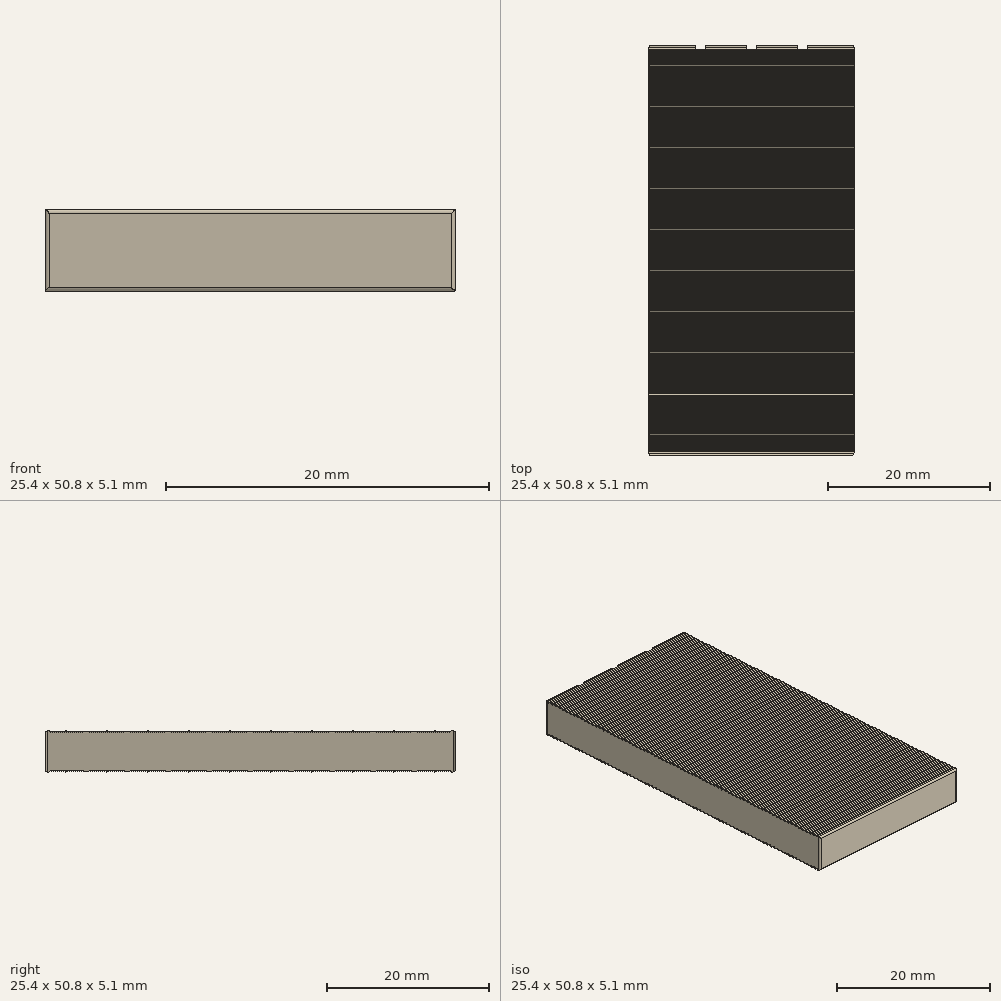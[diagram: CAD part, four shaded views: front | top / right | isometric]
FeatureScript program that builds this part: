
annotation { "Feature Type Name" : "Feature", "Feature Type Description" : "" }
export const myFeature = defineFeature(function(context is Context, id is Id, definition is map)
    precondition{}
    {
        {
            var Q0;
            Q0=qCreatedBy(makeId("Front.planeOp"),FACE);
            var sketch = newSketch(context, id + "F0", { "sketchPlane" : qUnion([Q0])});
            skLineSegment(sketch, "E0.bottom", {"start": v(12.7, -2.54) * mm, "end": v(-12.7, -2.54) * mm});
            skLineSegment(sketch, "E0.top", {"start": v(12.7, 2.54) * mm, "end": v(-12.7, 2.54) * mm});
            skLineSegment(sketch, "E0.left", {"start": v(12.7, -2.54) * mm, "end": v(12.7, 2.54) * mm});
            skLineSegment(sketch, "E0.right", {"start": v(-12.7, -2.54) * mm, "end": v(-12.7, 2.54) * mm});
            skPoint(sketch, "E0.middle", {"position": v(0, 0) * mm});
            skSolve(sketch);
        }
        {
            var Q0;
            Q0 = qSketchRegion(id + "F0", true);
            extrude(context, id + "F1", {"entities" : qUnion([Q0]), "endBound" : BoundingType.SYMMETRIC, "depth" : 50.8 * mm, "offsetDistance" : 25.4 * mm});
        }
        {
            var Q0;
            Q0=qCreatedBy(makeId("Right.planeOp"),FACE);
            var sketch = newSketch(context, id + "F2", { "sketchPlane" : qUnion([Q0])});
            skLineSegment(sketch, "E1", {"start": v(0, -2.54) * mm, "end": v(-0.13, -2.32) * mm});
            skLineSegment(sketch, "E2", {"start": v(-0.13, -2.32) * mm, "end": v(-0.25, -2.54) * mm});
            skLineSegment(sketch, "E3.1.0.0", {"start": v(0.25, -2.54) * mm, "end": v(0.13, -2.32) * mm});
            skLineSegment(sketch, "E3.1.0.1", {"start": v(0.13, -2.32) * mm, "end": v(0, -2.54) * mm});
            skLineSegment(sketch, "E3.2.0.0", {"start": v(0.5, -2.54) * mm, "end": v(0.38, -2.32) * mm});
            skLineSegment(sketch, "E3.2.0.1", {"start": v(0.38, -2.32) * mm, "end": v(0.25, -2.54) * mm});
            skLineSegment(sketch, "E3.3.0.0", {"start": v(0.76, -2.54) * mm, "end": v(0.64, -2.32) * mm});
            skLineSegment(sketch, "E3.3.0.1", {"start": v(0.64, -2.32) * mm, "end": v(0.5, -2.54) * mm});
            skLineSegment(sketch, "E3.4.0.0", {"start": v(1.02, -2.54) * mm, "end": v(0.89, -2.32) * mm});
            skLineSegment(sketch, "E3.4.0.1", {"start": v(0.89, -2.32) * mm, "end": v(0.76, -2.54) * mm});
            skLineSegment(sketch, "E3.5.0.0", {"start": v(1.27, -2.54) * mm, "end": v(1.14, -2.32) * mm});
            skLineSegment(sketch, "E3.5.0.1", {"start": v(1.14, -2.32) * mm, "end": v(1.02, -2.54) * mm});
            skLineSegment(sketch, "E3.6.0.0", {"start": v(1.52, -2.54) * mm, "end": v(1.4, -2.32) * mm});
            skLineSegment(sketch, "E3.6.0.1", {"start": v(1.4, -2.32) * mm, "end": v(1.27, -2.54) * mm});
            skLineSegment(sketch, "E3.7.0.0", {"start": v(1.78, -2.54) * mm, "end": v(1.65, -2.32) * mm});
            skLineSegment(sketch, "E3.7.0.1", {"start": v(1.65, -2.32) * mm, "end": v(1.52, -2.54) * mm});
            skLineSegment(sketch, "E3.8.0.0", {"start": v(2.03, -2.54) * mm, "end": v(1.9, -2.32) * mm});
            skLineSegment(sketch, "E3.8.0.1", {"start": v(1.9, -2.32) * mm, "end": v(1.78, -2.54) * mm});
            skLineSegment(sketch, "E3.9.0.0", {"start": v(2.29, -2.54) * mm, "end": v(2.16, -2.32) * mm});
            skLineSegment(sketch, "E3.9.0.1", {"start": v(2.16, -2.32) * mm, "end": v(2.03, -2.54) * mm});
            skLineSegment(sketch, "E3.10.0.0", {"start": v(2.54, -2.54) * mm, "end": v(2.41, -2.32) * mm});
            skLineSegment(sketch, "E3.10.0.1", {"start": v(2.41, -2.32) * mm, "end": v(2.29, -2.54) * mm});
            skLineSegment(sketch, "E3.11.0.0", {"start": v(2.8, -2.54) * mm, "end": v(2.67, -2.32) * mm});
            skLineSegment(sketch, "E3.11.0.1", {"start": v(2.67, -2.32) * mm, "end": v(2.54, -2.54) * mm});
            skLineSegment(sketch, "E3.12.0.0", {"start": v(3.05, -2.54) * mm, "end": v(2.92, -2.32) * mm});
            skLineSegment(sketch, "E3.12.0.1", {"start": v(2.92, -2.32) * mm, "end": v(2.8, -2.54) * mm});
            skLineSegment(sketch, "E3.13.0.0", {"start": v(3.3, -2.54) * mm, "end": v(3.18, -2.32) * mm});
            skLineSegment(sketch, "E3.13.0.1", {"start": v(3.18, -2.32) * mm, "end": v(3.05, -2.54) * mm});
            skLineSegment(sketch, "E3.14.0.0", {"start": v(3.56, -2.54) * mm, "end": v(3.43, -2.32) * mm});
            skLineSegment(sketch, "E3.14.0.1", {"start": v(3.43, -2.32) * mm, "end": v(3.3, -2.54) * mm});
            skLineSegment(sketch, "E3.15.0.0", {"start": v(3.81, -2.54) * mm, "end": v(3.68, -2.32) * mm});
            skLineSegment(sketch, "E3.15.0.1", {"start": v(3.68, -2.32) * mm, "end": v(3.56, -2.54) * mm});
            skLineSegment(sketch, "E3.16.0.0", {"start": v(4.06, -2.54) * mm, "end": v(3.94, -2.32) * mm});
            skLineSegment(sketch, "E3.16.0.1", {"start": v(3.94, -2.32) * mm, "end": v(3.81, -2.54) * mm});
            skLineSegment(sketch, "E3.17.0.0", {"start": v(4.32, -2.54) * mm, "end": v(4.2, -2.32) * mm});
            skLineSegment(sketch, "E3.17.0.1", {"start": v(4.2, -2.32) * mm, "end": v(4.06, -2.54) * mm});
            skLineSegment(sketch, "E3.18.0.0", {"start": v(4.57, -2.54) * mm, "end": v(4.45, -2.32) * mm});
            skLineSegment(sketch, "E3.18.0.1", {"start": v(4.45, -2.32) * mm, "end": v(4.32, -2.54) * mm});
            skLineSegment(sketch, "E3.19.0.0", {"start": v(4.83, -2.54) * mm, "end": v(4.7, -2.32) * mm});
            skLineSegment(sketch, "E3.19.0.1", {"start": v(4.7, -2.32) * mm, "end": v(4.57, -2.54) * mm});
            skLineSegment(sketch, "E3.20.0.0", {"start": v(5.08, -2.54) * mm, "end": v(4.95, -2.32) * mm});
            skLineSegment(sketch, "E3.20.0.1", {"start": v(4.95, -2.32) * mm, "end": v(4.83, -2.54) * mm});
            skLineSegment(sketch, "E3.21.0.0", {"start": v(5.33, -2.54) * mm, "end": v(5.2, -2.32) * mm});
            skLineSegment(sketch, "E3.21.0.1", {"start": v(5.2, -2.32) * mm, "end": v(5.08, -2.54) * mm});
            skLineSegment(sketch, "E3.22.0.0", {"start": v(5.59, -2.54) * mm, "end": v(5.46, -2.32) * mm});
            skLineSegment(sketch, "E3.22.0.1", {"start": v(5.46, -2.32) * mm, "end": v(5.33, -2.54) * mm});
            skLineSegment(sketch, "E3.23.0.0", {"start": v(5.84, -2.54) * mm, "end": v(5.72, -2.32) * mm});
            skLineSegment(sketch, "E3.23.0.1", {"start": v(5.72, -2.32) * mm, "end": v(5.59, -2.54) * mm});
            skLineSegment(sketch, "E3.24.0.0", {"start": v(6.1, -2.54) * mm, "end": v(5.97, -2.32) * mm});
            skLineSegment(sketch, "E3.24.0.1", {"start": v(5.97, -2.32) * mm, "end": v(5.84, -2.54) * mm});
            skLineSegment(sketch, "E3.25.0.0", {"start": v(6.35, -2.54) * mm, "end": v(6.22, -2.32) * mm});
            skLineSegment(sketch, "E3.25.0.1", {"start": v(6.22, -2.32) * mm, "end": v(6.1, -2.54) * mm});
            skLineSegment(sketch, "E3.26.0.0", {"start": v(6.6, -2.54) * mm, "end": v(6.48, -2.32) * mm});
            skLineSegment(sketch, "E3.26.0.1", {"start": v(6.48, -2.32) * mm, "end": v(6.35, -2.54) * mm});
            skLineSegment(sketch, "E3.27.0.0", {"start": v(6.86, -2.54) * mm, "end": v(6.73, -2.32) * mm});
            skLineSegment(sketch, "E3.27.0.1", {"start": v(6.73, -2.32) * mm, "end": v(6.6, -2.54) * mm});
            skLineSegment(sketch, "E3.28.0.0", {"start": v(7.11, -2.54) * mm, "end": v(6.99, -2.32) * mm});
            skLineSegment(sketch, "E3.28.0.1", {"start": v(6.99, -2.32) * mm, "end": v(6.86, -2.54) * mm});
            skLineSegment(sketch, "E3.29.0.0", {"start": v(7.37, -2.54) * mm, "end": v(7.24, -2.32) * mm});
            skLineSegment(sketch, "E3.29.0.1", {"start": v(7.24, -2.32) * mm, "end": v(7.11, -2.54) * mm});
            skLineSegment(sketch, "E3.30.0.0", {"start": v(7.62, -2.54) * mm, "end": v(7.5, -2.32) * mm});
            skLineSegment(sketch, "E3.30.0.1", {"start": v(7.5, -2.32) * mm, "end": v(7.37, -2.54) * mm});
            skLineSegment(sketch, "E3.31.0.0", {"start": v(7.87, -2.54) * mm, "end": v(7.75, -2.32) * mm});
            skLineSegment(sketch, "E3.31.0.1", {"start": v(7.75, -2.32) * mm, "end": v(7.62, -2.54) * mm});
            skLineSegment(sketch, "E3.32.0.0", {"start": v(8.13, -2.54) * mm, "end": v(8, -2.32) * mm});
            skLineSegment(sketch, "E3.32.0.1", {"start": v(8, -2.32) * mm, "end": v(7.87, -2.54) * mm});
            skLineSegment(sketch, "E3.33.0.0", {"start": v(8.38, -2.54) * mm, "end": v(8.26, -2.32) * mm});
            skLineSegment(sketch, "E3.33.0.1", {"start": v(8.26, -2.32) * mm, "end": v(8.13, -2.54) * mm});
            skLineSegment(sketch, "E3.34.0.0", {"start": v(8.64, -2.54) * mm, "end": v(8.5, -2.32) * mm});
            skLineSegment(sketch, "E3.34.0.1", {"start": v(8.5, -2.32) * mm, "end": v(8.38, -2.54) * mm});
            skLineSegment(sketch, "E3.35.0.0", {"start": v(8.9, -2.54) * mm, "end": v(8.76, -2.32) * mm});
            skLineSegment(sketch, "E3.35.0.1", {"start": v(8.76, -2.32) * mm, "end": v(8.64, -2.54) * mm});
            skLineSegment(sketch, "E3.36.0.0", {"start": v(9.14, -2.54) * mm, "end": v(9.02, -2.32) * mm});
            skLineSegment(sketch, "E3.36.0.1", {"start": v(9.02, -2.32) * mm, "end": v(8.9, -2.54) * mm});
            skLineSegment(sketch, "E3.37.0.0", {"start": v(9.4, -2.54) * mm, "end": v(9.27, -2.32) * mm});
            skLineSegment(sketch, "E3.37.0.1", {"start": v(9.27, -2.32) * mm, "end": v(9.14, -2.54) * mm});
            skLineSegment(sketch, "E3.38.0.0", {"start": v(9.65, -2.54) * mm, "end": v(9.53, -2.32) * mm});
            skLineSegment(sketch, "E3.38.0.1", {"start": v(9.53, -2.32) * mm, "end": v(9.4, -2.54) * mm});
            skLineSegment(sketch, "E3.39.0.0", {"start": v(9.9, -2.54) * mm, "end": v(9.78, -2.32) * mm});
            skLineSegment(sketch, "E3.39.0.1", {"start": v(9.78, -2.32) * mm, "end": v(9.65, -2.54) * mm});
            skLineSegment(sketch, "E3.40.0.0", {"start": v(10.16, -2.54) * mm, "end": v(10.03, -2.32) * mm});
            skLineSegment(sketch, "E3.40.0.1", {"start": v(10.03, -2.32) * mm, "end": v(9.9, -2.54) * mm});
            skLineSegment(sketch, "E3.41.0.0", {"start": v(10.41, -2.54) * mm, "end": v(10.29, -2.32) * mm});
            skLineSegment(sketch, "E3.41.0.1", {"start": v(10.29, -2.32) * mm, "end": v(10.16, -2.54) * mm});
            skLineSegment(sketch, "E3.42.0.0", {"start": v(10.67, -2.54) * mm, "end": v(10.54, -2.32) * mm});
            skLineSegment(sketch, "E3.42.0.1", {"start": v(10.54, -2.32) * mm, "end": v(10.41, -2.54) * mm});
            skLineSegment(sketch, "E3.43.0.0", {"start": v(10.92, -2.54) * mm, "end": v(10.8, -2.32) * mm});
            skLineSegment(sketch, "E3.43.0.1", {"start": v(10.8, -2.32) * mm, "end": v(10.67, -2.54) * mm});
            skLineSegment(sketch, "E3.44.0.0", {"start": v(11.18, -2.54) * mm, "end": v(11.05, -2.32) * mm});
            skLineSegment(sketch, "E3.44.0.1", {"start": v(11.05, -2.32) * mm, "end": v(10.92, -2.54) * mm});
            skLineSegment(sketch, "E3.45.0.0", {"start": v(11.43, -2.54) * mm, "end": v(11.3, -2.32) * mm});
            skLineSegment(sketch, "E3.45.0.1", {"start": v(11.3, -2.32) * mm, "end": v(11.18, -2.54) * mm});
            skLineSegment(sketch, "E3.46.0.0", {"start": v(11.68, -2.54) * mm, "end": v(11.56, -2.32) * mm});
            skLineSegment(sketch, "E3.46.0.1", {"start": v(11.56, -2.32) * mm, "end": v(11.43, -2.54) * mm});
            skLineSegment(sketch, "E3.47.0.0", {"start": v(11.94, -2.54) * mm, "end": v(11.81, -2.32) * mm});
            skLineSegment(sketch, "E3.47.0.1", {"start": v(11.81, -2.32) * mm, "end": v(11.68, -2.54) * mm});
            skLineSegment(sketch, "E3.48.0.0", {"start": v(12.2, -2.54) * mm, "end": v(12.07, -2.32) * mm});
            skLineSegment(sketch, "E3.48.0.1", {"start": v(12.07, -2.32) * mm, "end": v(11.94, -2.54) * mm});
            skLineSegment(sketch, "E3.49.0.0", {"start": v(12.45, -2.54) * mm, "end": v(12.32, -2.32) * mm});
            skLineSegment(sketch, "E3.49.0.1", {"start": v(12.32, -2.32) * mm, "end": v(12.2, -2.54) * mm});
            skLineSegment(sketch, "E3.direction1", {"start": v(-0.25, -2.54) * mm, "end": v(0, -2.54) * mm, "construction": true});
            skLineSegment(sketch, "E4.0.50.0", {"start": v(12.7, -2.54) * mm, "end": v(12.57, -2.32) * mm});
            skLineSegment(sketch, "E4.3.50.0", {"start": v(12.57, -2.32) * mm, "end": v(12.45, -2.54) * mm});
            skLineSegment(sketch, "E4.0.51.0", {"start": v(12.95, -2.54) * mm, "end": v(12.83, -2.32) * mm});
            skLineSegment(sketch, "E4.3.51.0", {"start": v(12.83, -2.32) * mm, "end": v(12.7, -2.54) * mm});
            skLineSegment(sketch, "E4.0.52.0", {"start": v(13.2, -2.54) * mm, "end": v(13.08, -2.32) * mm});
            skLineSegment(sketch, "E4.3.52.0", {"start": v(13.08, -2.32) * mm, "end": v(12.95, -2.54) * mm});
            skLineSegment(sketch, "E4.0.53.0", {"start": v(13.46, -2.54) * mm, "end": v(13.34, -2.32) * mm});
            skLineSegment(sketch, "E4.3.53.0", {"start": v(13.34, -2.32) * mm, "end": v(13.2, -2.54) * mm});
            skLineSegment(sketch, "E4.0.54.0", {"start": v(13.72, -2.54) * mm, "end": v(13.59, -2.32) * mm});
            skLineSegment(sketch, "E4.3.54.0", {"start": v(13.59, -2.32) * mm, "end": v(13.46, -2.54) * mm});
            skLineSegment(sketch, "E4.0.55.0", {"start": v(13.97, -2.54) * mm, "end": v(13.84, -2.32) * mm});
            skLineSegment(sketch, "E4.3.55.0", {"start": v(13.84, -2.32) * mm, "end": v(13.72, -2.54) * mm});
            skLineSegment(sketch, "E4.0.56.0", {"start": v(14.22, -2.54) * mm, "end": v(14.1, -2.32) * mm});
            skLineSegment(sketch, "E4.3.56.0", {"start": v(14.1, -2.32) * mm, "end": v(13.97, -2.54) * mm});
            skLineSegment(sketch, "E4.0.57.0", {"start": v(14.48, -2.54) * mm, "end": v(14.35, -2.32) * mm});
            skLineSegment(sketch, "E4.3.57.0", {"start": v(14.35, -2.32) * mm, "end": v(14.22, -2.54) * mm});
            skLineSegment(sketch, "E4.0.58.0", {"start": v(14.73, -2.54) * mm, "end": v(14.6, -2.32) * mm});
            skLineSegment(sketch, "E4.3.58.0", {"start": v(14.6, -2.32) * mm, "end": v(14.48, -2.54) * mm});
            skLineSegment(sketch, "E4.0.59.0", {"start": v(14.99, -2.54) * mm, "end": v(14.86, -2.32) * mm});
            skLineSegment(sketch, "E4.3.59.0", {"start": v(14.86, -2.32) * mm, "end": v(14.73, -2.54) * mm});
            skLineSegment(sketch, "E4.0.60.0", {"start": v(15.24, -2.54) * mm, "end": v(15.11, -2.32) * mm});
            skLineSegment(sketch, "E4.3.60.0", {"start": v(15.11, -2.32) * mm, "end": v(14.99, -2.54) * mm});
            skLineSegment(sketch, "E4.0.61.0", {"start": v(15.5, -2.54) * mm, "end": v(15.37, -2.32) * mm});
            skLineSegment(sketch, "E4.3.61.0", {"start": v(15.37, -2.32) * mm, "end": v(15.24, -2.54) * mm});
            skLineSegment(sketch, "E4.0.62.0", {"start": v(15.75, -2.54) * mm, "end": v(15.62, -2.32) * mm});
            skLineSegment(sketch, "E4.3.62.0", {"start": v(15.62, -2.32) * mm, "end": v(15.5, -2.54) * mm});
            skLineSegment(sketch, "E4.0.63.0", {"start": v(16, -2.54) * mm, "end": v(15.88, -2.32) * mm});
            skLineSegment(sketch, "E4.3.63.0", {"start": v(15.88, -2.32) * mm, "end": v(15.75, -2.54) * mm});
            skLineSegment(sketch, "E4.0.64.0", {"start": v(16.26, -2.54) * mm, "end": v(16.13, -2.32) * mm});
            skLineSegment(sketch, "E4.3.64.0", {"start": v(16.13, -2.32) * mm, "end": v(16, -2.54) * mm});
            skLineSegment(sketch, "E4.0.65.0", {"start": v(16.51, -2.54) * mm, "end": v(16.38, -2.32) * mm});
            skLineSegment(sketch, "E4.3.65.0", {"start": v(16.38, -2.32) * mm, "end": v(16.26, -2.54) * mm});
            skLineSegment(sketch, "E4.0.66.0", {"start": v(16.76, -2.54) * mm, "end": v(16.64, -2.32) * mm});
            skLineSegment(sketch, "E4.3.66.0", {"start": v(16.64, -2.32) * mm, "end": v(16.51, -2.54) * mm});
            skLineSegment(sketch, "E4.0.67.0", {"start": v(17.02, -2.54) * mm, "end": v(16.9, -2.32) * mm});
            skLineSegment(sketch, "E4.3.67.0", {"start": v(16.9, -2.32) * mm, "end": v(16.76, -2.54) * mm});
            skLineSegment(sketch, "E4.0.68.0", {"start": v(17.27, -2.54) * mm, "end": v(17.15, -2.32) * mm});
            skLineSegment(sketch, "E4.3.68.0", {"start": v(17.15, -2.32) * mm, "end": v(17.02, -2.54) * mm});
            skLineSegment(sketch, "E4.0.69.0", {"start": v(17.53, -2.54) * mm, "end": v(17.4, -2.32) * mm});
            skLineSegment(sketch, "E4.3.69.0", {"start": v(17.4, -2.32) * mm, "end": v(17.27, -2.54) * mm});
            skLineSegment(sketch, "E4.0.70.0", {"start": v(17.78, -2.54) * mm, "end": v(17.65, -2.32) * mm});
            skLineSegment(sketch, "E4.3.70.0", {"start": v(17.65, -2.32) * mm, "end": v(17.53, -2.54) * mm});
            skLineSegment(sketch, "E4.0.71.0", {"start": v(18.03, -2.54) * mm, "end": v(17.9, -2.32) * mm});
            skLineSegment(sketch, "E4.3.71.0", {"start": v(17.9, -2.32) * mm, "end": v(17.78, -2.54) * mm});
            skLineSegment(sketch, "E4.0.72.0", {"start": v(18.29, -2.54) * mm, "end": v(18.16, -2.32) * mm});
            skLineSegment(sketch, "E4.3.72.0", {"start": v(18.16, -2.32) * mm, "end": v(18.03, -2.54) * mm});
            skLineSegment(sketch, "E4.0.73.0", {"start": v(18.54, -2.54) * mm, "end": v(18.42, -2.32) * mm});
            skLineSegment(sketch, "E4.3.73.0", {"start": v(18.42, -2.32) * mm, "end": v(18.29, -2.54) * mm});
            skLineSegment(sketch, "E4.0.74.0", {"start": v(18.8, -2.54) * mm, "end": v(18.67, -2.32) * mm});
            skLineSegment(sketch, "E4.3.74.0", {"start": v(18.67, -2.32) * mm, "end": v(18.54, -2.54) * mm});
            skLineSegment(sketch, "E5.0.75.0", {"start": v(19.05, -2.54) * mm, "end": v(18.92, -2.32) * mm});
            skLineSegment(sketch, "E5.3.75.0", {"start": v(18.92, -2.32) * mm, "end": v(18.8, -2.54) * mm});
            skLineSegment(sketch, "E5.0.76.0", {"start": v(19.3, -2.54) * mm, "end": v(19.18, -2.32) * mm});
            skLineSegment(sketch, "E5.3.76.0", {"start": v(19.18, -2.32) * mm, "end": v(19.05, -2.54) * mm});
            skLineSegment(sketch, "E6.1.0.0", {"start": v(-0.25, -2.54) * mm, "end": v(-0.38, -2.32) * mm});
            skLineSegment(sketch, "E6.1.0.1", {"start": v(-0.38, -2.32) * mm, "end": v(-0.5, -2.54) * mm});
            skLineSegment(sketch, "E6.2.0.0", {"start": v(-0.5, -2.54) * mm, "end": v(-0.63, -2.32) * mm});
            skLineSegment(sketch, "E6.2.0.1", {"start": v(-0.63, -2.32) * mm, "end": v(-0.76, -2.54) * mm});
            skLineSegment(sketch, "E6.3.0.0", {"start": v(-0.76, -2.54) * mm, "end": v(-0.89, -2.32) * mm});
            skLineSegment(sketch, "E6.3.0.1", {"start": v(-0.89, -2.32) * mm, "end": v(-1.02, -2.54) * mm});
            skLineSegment(sketch, "E6.4.0.0", {"start": v(-1.02, -2.54) * mm, "end": v(-1.14, -2.32) * mm});
            skLineSegment(sketch, "E6.4.0.1", {"start": v(-1.14, -2.32) * mm, "end": v(-1.27, -2.54) * mm});
            skLineSegment(sketch, "E6.5.0.0", {"start": v(-1.27, -2.54) * mm, "end": v(-1.4, -2.32) * mm});
            skLineSegment(sketch, "E6.5.0.1", {"start": v(-1.4, -2.32) * mm, "end": v(-1.52, -2.54) * mm});
            skLineSegment(sketch, "E6.6.0.0", {"start": v(-1.52, -2.54) * mm, "end": v(-1.65, -2.32) * mm});
            skLineSegment(sketch, "E6.6.0.1", {"start": v(-1.65, -2.32) * mm, "end": v(-1.78, -2.54) * mm});
            skLineSegment(sketch, "E6.7.0.0", {"start": v(-1.78, -2.54) * mm, "end": v(-1.9, -2.32) * mm});
            skLineSegment(sketch, "E6.7.0.1", {"start": v(-1.9, -2.32) * mm, "end": v(-2.03, -2.54) * mm});
            skLineSegment(sketch, "E6.8.0.0", {"start": v(-2.03, -2.54) * mm, "end": v(-2.16, -2.32) * mm});
            skLineSegment(sketch, "E6.8.0.1", {"start": v(-2.16, -2.32) * mm, "end": v(-2.29, -2.54) * mm});
            skLineSegment(sketch, "E6.9.0.0", {"start": v(-2.29, -2.54) * mm, "end": v(-2.41, -2.32) * mm});
            skLineSegment(sketch, "E6.9.0.1", {"start": v(-2.41, -2.32) * mm, "end": v(-2.54, -2.54) * mm});
            skLineSegment(sketch, "E6.10.0.0", {"start": v(-2.54, -2.54) * mm, "end": v(-2.67, -2.32) * mm});
            skLineSegment(sketch, "E6.10.0.1", {"start": v(-2.67, -2.32) * mm, "end": v(-2.8, -2.54) * mm});
            skLineSegment(sketch, "E6.11.0.0", {"start": v(-2.8, -2.54) * mm, "end": v(-2.92, -2.32) * mm});
            skLineSegment(sketch, "E6.11.0.1", {"start": v(-2.92, -2.32) * mm, "end": v(-3.05, -2.54) * mm});
            skLineSegment(sketch, "E6.12.0.0", {"start": v(-3.05, -2.54) * mm, "end": v(-3.17, -2.32) * mm});
            skLineSegment(sketch, "E6.12.0.1", {"start": v(-3.17, -2.32) * mm, "end": v(-3.3, -2.54) * mm});
            skLineSegment(sketch, "E6.13.0.0", {"start": v(-3.3, -2.54) * mm, "end": v(-3.43, -2.32) * mm});
            skLineSegment(sketch, "E6.13.0.1", {"start": v(-3.43, -2.32) * mm, "end": v(-3.56, -2.54) * mm});
            skLineSegment(sketch, "E6.14.0.0", {"start": v(-3.56, -2.54) * mm, "end": v(-3.68, -2.32) * mm});
            skLineSegment(sketch, "E6.14.0.1", {"start": v(-3.68, -2.32) * mm, "end": v(-3.8, -2.54) * mm});
            skLineSegment(sketch, "E6.15.0.0", {"start": v(-3.8, -2.54) * mm, "end": v(-3.94, -2.32) * mm});
            skLineSegment(sketch, "E6.15.0.1", {"start": v(-3.94, -2.32) * mm, "end": v(-4.06, -2.54) * mm});
            skLineSegment(sketch, "E6.16.0.0", {"start": v(-4.06, -2.54) * mm, "end": v(-4.2, -2.32) * mm});
            skLineSegment(sketch, "E6.16.0.1", {"start": v(-4.2, -2.32) * mm, "end": v(-4.32, -2.54) * mm});
            skLineSegment(sketch, "E6.17.0.0", {"start": v(-4.32, -2.54) * mm, "end": v(-4.44, -2.32) * mm});
            skLineSegment(sketch, "E6.17.0.1", {"start": v(-4.44, -2.32) * mm, "end": v(-4.57, -2.54) * mm});
            skLineSegment(sketch, "E6.18.0.0", {"start": v(-4.57, -2.54) * mm, "end": v(-4.7, -2.32) * mm});
            skLineSegment(sketch, "E6.18.0.1", {"start": v(-4.7, -2.32) * mm, "end": v(-4.83, -2.54) * mm});
            skLineSegment(sketch, "E6.19.0.0", {"start": v(-4.83, -2.54) * mm, "end": v(-4.95, -2.32) * mm});
            skLineSegment(sketch, "E6.19.0.1", {"start": v(-4.95, -2.32) * mm, "end": v(-5.08, -2.54) * mm});
            skLineSegment(sketch, "E6.20.0.0", {"start": v(-5.08, -2.54) * mm, "end": v(-5.2, -2.32) * mm});
            skLineSegment(sketch, "E6.20.0.1", {"start": v(-5.2, -2.32) * mm, "end": v(-5.33, -2.54) * mm});
            skLineSegment(sketch, "E6.21.0.0", {"start": v(-5.33, -2.54) * mm, "end": v(-5.46, -2.32) * mm});
            skLineSegment(sketch, "E6.21.0.1", {"start": v(-5.46, -2.32) * mm, "end": v(-5.59, -2.54) * mm});
            skLineSegment(sketch, "E6.22.0.0", {"start": v(-5.59, -2.54) * mm, "end": v(-5.71, -2.32) * mm});
            skLineSegment(sketch, "E6.22.0.1", {"start": v(-5.71, -2.32) * mm, "end": v(-5.84, -2.54) * mm});
            skLineSegment(sketch, "E6.23.0.0", {"start": v(-5.84, -2.54) * mm, "end": v(-5.97, -2.32) * mm});
            skLineSegment(sketch, "E6.23.0.1", {"start": v(-5.97, -2.32) * mm, "end": v(-6.1, -2.54) * mm});
            skLineSegment(sketch, "E6.24.0.0", {"start": v(-6.1, -2.54) * mm, "end": v(-6.22, -2.32) * mm});
            skLineSegment(sketch, "E6.24.0.1", {"start": v(-6.22, -2.32) * mm, "end": v(-6.35, -2.54) * mm});
            skLineSegment(sketch, "E6.25.0.0", {"start": v(-6.35, -2.54) * mm, "end": v(-6.48, -2.32) * mm});
            skLineSegment(sketch, "E6.25.0.1", {"start": v(-6.48, -2.32) * mm, "end": v(-6.6, -2.54) * mm});
            skLineSegment(sketch, "E6.26.0.0", {"start": v(-6.6, -2.54) * mm, "end": v(-6.73, -2.32) * mm});
            skLineSegment(sketch, "E6.26.0.1", {"start": v(-6.73, -2.32) * mm, "end": v(-6.86, -2.54) * mm});
            skLineSegment(sketch, "E6.27.0.0", {"start": v(-6.86, -2.54) * mm, "end": v(-6.98, -2.32) * mm});
            skLineSegment(sketch, "E6.27.0.1", {"start": v(-6.98, -2.32) * mm, "end": v(-7.11, -2.54) * mm});
            skLineSegment(sketch, "E6.28.0.0", {"start": v(-7.11, -2.54) * mm, "end": v(-7.24, -2.32) * mm});
            skLineSegment(sketch, "E6.28.0.1", {"start": v(-7.24, -2.32) * mm, "end": v(-7.37, -2.54) * mm});
            skLineSegment(sketch, "E6.29.0.0", {"start": v(-7.37, -2.54) * mm, "end": v(-7.5, -2.32) * mm});
            skLineSegment(sketch, "E6.29.0.1", {"start": v(-7.5, -2.32) * mm, "end": v(-7.62, -2.54) * mm});
            skLineSegment(sketch, "E6.30.0.0", {"start": v(-7.62, -2.54) * mm, "end": v(-7.75, -2.32) * mm});
            skLineSegment(sketch, "E6.30.0.1", {"start": v(-7.75, -2.32) * mm, "end": v(-7.87, -2.54) * mm});
            skLineSegment(sketch, "E6.31.0.0", {"start": v(-7.87, -2.54) * mm, "end": v(-8, -2.32) * mm});
            skLineSegment(sketch, "E6.31.0.1", {"start": v(-8, -2.32) * mm, "end": v(-8.13, -2.54) * mm});
            skLineSegment(sketch, "E6.32.0.0", {"start": v(-8.13, -2.54) * mm, "end": v(-8.25, -2.32) * mm});
            skLineSegment(sketch, "E6.32.0.1", {"start": v(-8.25, -2.32) * mm, "end": v(-8.38, -2.54) * mm});
            skLineSegment(sketch, "E6.33.0.0", {"start": v(-8.38, -2.54) * mm, "end": v(-8.5, -2.32) * mm});
            skLineSegment(sketch, "E6.33.0.1", {"start": v(-8.5, -2.32) * mm, "end": v(-8.64, -2.54) * mm});
            skLineSegment(sketch, "E6.34.0.0", {"start": v(-8.64, -2.54) * mm, "end": v(-8.76, -2.32) * mm});
            skLineSegment(sketch, "E6.34.0.1", {"start": v(-8.76, -2.32) * mm, "end": v(-8.89, -2.54) * mm});
            skLineSegment(sketch, "E6.35.0.0", {"start": v(-8.89, -2.54) * mm, "end": v(-9.02, -2.32) * mm});
            skLineSegment(sketch, "E6.35.0.1", {"start": v(-9.02, -2.32) * mm, "end": v(-9.14, -2.54) * mm});
            skLineSegment(sketch, "E6.36.0.0", {"start": v(-9.14, -2.54) * mm, "end": v(-9.27, -2.32) * mm});
            skLineSegment(sketch, "E6.36.0.1", {"start": v(-9.27, -2.32) * mm, "end": v(-9.4, -2.54) * mm});
            skLineSegment(sketch, "E6.37.0.0", {"start": v(-9.4, -2.54) * mm, "end": v(-9.52, -2.32) * mm});
            skLineSegment(sketch, "E6.37.0.1", {"start": v(-9.52, -2.32) * mm, "end": v(-9.65, -2.54) * mm});
            skLineSegment(sketch, "E6.38.0.0", {"start": v(-9.65, -2.54) * mm, "end": v(-9.78, -2.32) * mm});
            skLineSegment(sketch, "E6.38.0.1", {"start": v(-9.78, -2.32) * mm, "end": v(-9.9, -2.54) * mm});
            skLineSegment(sketch, "E6.39.0.0", {"start": v(-9.9, -2.54) * mm, "end": v(-10.03, -2.32) * mm});
            skLineSegment(sketch, "E6.39.0.1", {"start": v(-10.03, -2.32) * mm, "end": v(-10.16, -2.54) * mm});
            skLineSegment(sketch, "E6.40.0.0", {"start": v(-10.16, -2.54) * mm, "end": v(-10.29, -2.32) * mm});
            skLineSegment(sketch, "E6.40.0.1", {"start": v(-10.29, -2.32) * mm, "end": v(-10.41, -2.54) * mm});
            skLineSegment(sketch, "E6.41.0.0", {"start": v(-10.41, -2.54) * mm, "end": v(-10.54, -2.32) * mm});
            skLineSegment(sketch, "E6.41.0.1", {"start": v(-10.54, -2.32) * mm, "end": v(-10.67, -2.54) * mm});
            skLineSegment(sketch, "E6.42.0.0", {"start": v(-10.67, -2.54) * mm, "end": v(-10.8, -2.32) * mm});
            skLineSegment(sketch, "E6.42.0.1", {"start": v(-10.8, -2.32) * mm, "end": v(-10.92, -2.54) * mm});
            skLineSegment(sketch, "E6.43.0.0", {"start": v(-10.92, -2.54) * mm, "end": v(-11.05, -2.32) * mm});
            skLineSegment(sketch, "E6.43.0.1", {"start": v(-11.05, -2.32) * mm, "end": v(-11.18, -2.54) * mm});
            skLineSegment(sketch, "E6.44.0.0", {"start": v(-11.18, -2.54) * mm, "end": v(-11.3, -2.32) * mm});
            skLineSegment(sketch, "E6.44.0.1", {"start": v(-11.3, -2.32) * mm, "end": v(-11.43, -2.54) * mm});
            skLineSegment(sketch, "E6.45.0.0", {"start": v(-11.43, -2.54) * mm, "end": v(-11.56, -2.32) * mm});
            skLineSegment(sketch, "E6.45.0.1", {"start": v(-11.56, -2.32) * mm, "end": v(-11.68, -2.54) * mm});
            skLineSegment(sketch, "E6.46.0.0", {"start": v(-11.68, -2.54) * mm, "end": v(-11.81, -2.32) * mm});
            skLineSegment(sketch, "E6.46.0.1", {"start": v(-11.81, -2.32) * mm, "end": v(-11.94, -2.54) * mm});
            skLineSegment(sketch, "E6.47.0.0", {"start": v(-11.94, -2.54) * mm, "end": v(-12.06, -2.32) * mm});
            skLineSegment(sketch, "E6.47.0.1", {"start": v(-12.06, -2.32) * mm, "end": v(-12.2, -2.54) * mm});
            skLineSegment(sketch, "E6.48.0.0", {"start": v(-12.2, -2.54) * mm, "end": v(-12.32, -2.32) * mm});
            skLineSegment(sketch, "E6.48.0.1", {"start": v(-12.32, -2.32) * mm, "end": v(-12.45, -2.54) * mm});
            skLineSegment(sketch, "E6.49.0.0", {"start": v(-12.45, -2.54) * mm, "end": v(-12.57, -2.32) * mm});
            skLineSegment(sketch, "E6.49.0.1", {"start": v(-12.57, -2.32) * mm, "end": v(-12.7, -2.54) * mm});
            skLineSegment(sketch, "E6.50.0.0", {"start": v(-12.7, -2.54) * mm, "end": v(-12.83, -2.32) * mm});
            skLineSegment(sketch, "E6.50.0.1", {"start": v(-12.83, -2.32) * mm, "end": v(-12.95, -2.54) * mm});
            skLineSegment(sketch, "E6.51.0.0", {"start": v(-12.95, -2.54) * mm, "end": v(-13.08, -2.32) * mm});
            skLineSegment(sketch, "E6.51.0.1", {"start": v(-13.08, -2.32) * mm, "end": v(-13.2, -2.54) * mm});
            skLineSegment(sketch, "E6.52.0.0", {"start": v(-13.2, -2.54) * mm, "end": v(-13.33, -2.32) * mm});
            skLineSegment(sketch, "E6.52.0.1", {"start": v(-13.33, -2.32) * mm, "end": v(-13.46, -2.54) * mm});
            skLineSegment(sketch, "E6.53.0.0", {"start": v(-13.46, -2.54) * mm, "end": v(-13.59, -2.32) * mm});
            skLineSegment(sketch, "E6.53.0.1", {"start": v(-13.59, -2.32) * mm, "end": v(-13.72, -2.54) * mm});
            skLineSegment(sketch, "E6.54.0.0", {"start": v(-13.72, -2.54) * mm, "end": v(-13.84, -2.32) * mm});
            skLineSegment(sketch, "E6.54.0.1", {"start": v(-13.84, -2.32) * mm, "end": v(-13.97, -2.54) * mm});
            skLineSegment(sketch, "E6.55.0.0", {"start": v(-13.97, -2.54) * mm, "end": v(-14.1, -2.32) * mm});
            skLineSegment(sketch, "E6.55.0.1", {"start": v(-14.1, -2.32) * mm, "end": v(-14.22, -2.54) * mm});
            skLineSegment(sketch, "E6.56.0.0", {"start": v(-14.22, -2.54) * mm, "end": v(-14.35, -2.32) * mm});
            skLineSegment(sketch, "E6.56.0.1", {"start": v(-14.35, -2.32) * mm, "end": v(-14.48, -2.54) * mm});
            skLineSegment(sketch, "E6.57.0.0", {"start": v(-14.48, -2.54) * mm, "end": v(-14.6, -2.32) * mm});
            skLineSegment(sketch, "E6.57.0.1", {"start": v(-14.6, -2.32) * mm, "end": v(-14.73, -2.54) * mm});
            skLineSegment(sketch, "E6.58.0.0", {"start": v(-14.73, -2.54) * mm, "end": v(-14.86, -2.32) * mm});
            skLineSegment(sketch, "E6.58.0.1", {"start": v(-14.86, -2.32) * mm, "end": v(-14.99, -2.54) * mm});
            skLineSegment(sketch, "E6.59.0.0", {"start": v(-14.99, -2.54) * mm, "end": v(-15.11, -2.32) * mm});
            skLineSegment(sketch, "E6.59.0.1", {"start": v(-15.11, -2.32) * mm, "end": v(-15.24, -2.54) * mm});
            skLineSegment(sketch, "E6.60.0.0", {"start": v(-15.24, -2.54) * mm, "end": v(-15.37, -2.32) * mm});
            skLineSegment(sketch, "E6.60.0.1", {"start": v(-15.37, -2.32) * mm, "end": v(-15.5, -2.54) * mm});
            skLineSegment(sketch, "E6.61.0.0", {"start": v(-15.5, -2.54) * mm, "end": v(-15.62, -2.32) * mm});
            skLineSegment(sketch, "E6.61.0.1", {"start": v(-15.62, -2.32) * mm, "end": v(-15.75, -2.54) * mm});
            skLineSegment(sketch, "E6.62.0.0", {"start": v(-15.75, -2.54) * mm, "end": v(-15.87, -2.32) * mm});
            skLineSegment(sketch, "E6.62.0.1", {"start": v(-15.87, -2.32) * mm, "end": v(-16, -2.54) * mm});
            skLineSegment(sketch, "E6.63.0.0", {"start": v(-16, -2.54) * mm, "end": v(-16.13, -2.32) * mm});
            skLineSegment(sketch, "E6.63.0.1", {"start": v(-16.13, -2.32) * mm, "end": v(-16.26, -2.54) * mm});
            skLineSegment(sketch, "E6.64.0.0", {"start": v(-16.26, -2.54) * mm, "end": v(-16.38, -2.32) * mm});
            skLineSegment(sketch, "E6.64.0.1", {"start": v(-16.38, -2.32) * mm, "end": v(-16.5, -2.54) * mm});
            skLineSegment(sketch, "E6.65.0.0", {"start": v(-16.5, -2.54) * mm, "end": v(-16.64, -2.32) * mm});
            skLineSegment(sketch, "E6.65.0.1", {"start": v(-16.64, -2.32) * mm, "end": v(-16.76, -2.54) * mm});
            skLineSegment(sketch, "E6.66.0.0", {"start": v(-16.76, -2.54) * mm, "end": v(-16.9, -2.32) * mm});
            skLineSegment(sketch, "E6.66.0.1", {"start": v(-16.9, -2.32) * mm, "end": v(-17.02, -2.54) * mm});
            skLineSegment(sketch, "E6.67.0.0", {"start": v(-17.02, -2.54) * mm, "end": v(-17.14, -2.32) * mm});
            skLineSegment(sketch, "E6.67.0.1", {"start": v(-17.14, -2.32) * mm, "end": v(-17.27, -2.54) * mm});
            skLineSegment(sketch, "E6.68.0.0", {"start": v(-17.27, -2.54) * mm, "end": v(-17.4, -2.32) * mm});
            skLineSegment(sketch, "E6.68.0.1", {"start": v(-17.4, -2.32) * mm, "end": v(-17.53, -2.54) * mm});
            skLineSegment(sketch, "E6.69.0.0", {"start": v(-17.53, -2.54) * mm, "end": v(-17.65, -2.32) * mm});
            skLineSegment(sketch, "E6.69.0.1", {"start": v(-17.65, -2.32) * mm, "end": v(-17.78, -2.54) * mm});
            skLineSegment(sketch, "E6.70.0.0", {"start": v(-17.78, -2.54) * mm, "end": v(-17.9, -2.32) * mm});
            skLineSegment(sketch, "E6.70.0.1", {"start": v(-17.9, -2.32) * mm, "end": v(-18.03, -2.54) * mm});
            skLineSegment(sketch, "E6.71.0.0", {"start": v(-18.03, -2.54) * mm, "end": v(-18.16, -2.32) * mm});
            skLineSegment(sketch, "E6.71.0.1", {"start": v(-18.16, -2.32) * mm, "end": v(-18.29, -2.54) * mm});
            skLineSegment(sketch, "E6.72.0.0", {"start": v(-18.29, -2.54) * mm, "end": v(-18.41, -2.32) * mm});
            skLineSegment(sketch, "E6.72.0.1", {"start": v(-18.41, -2.32) * mm, "end": v(-18.54, -2.54) * mm});
            skLineSegment(sketch, "E6.73.0.0", {"start": v(-18.54, -2.54) * mm, "end": v(-18.67, -2.32) * mm});
            skLineSegment(sketch, "E6.73.0.1", {"start": v(-18.67, -2.32) * mm, "end": v(-18.8, -2.54) * mm});
            skLineSegment(sketch, "E6.74.0.0", {"start": v(-18.8, -2.54) * mm, "end": v(-18.92, -2.32) * mm});
            skLineSegment(sketch, "E6.74.0.1", {"start": v(-18.92, -2.32) * mm, "end": v(-19.05, -2.54) * mm});
            skLineSegment(sketch, "E6.75.0.0", {"start": v(-19.05, -2.54) * mm, "end": v(-19.18, -2.32) * mm});
            skLineSegment(sketch, "E6.75.0.1", {"start": v(-19.18, -2.32) * mm, "end": v(-19.3, -2.54) * mm});
            skLineSegment(sketch, "E6.direction1", {"start": v(-0.25, -2.54) * mm, "end": v(-0.5, -2.54) * mm, "construction": true});
            skLineSegment(sketch, "E7.0.77.0", {"start": v(19.56, -2.54) * mm, "end": v(19.43, -2.32) * mm});
            skLineSegment(sketch, "E7.3.77.0", {"start": v(19.43, -2.32) * mm, "end": v(19.3, -2.54) * mm});
            skLineSegment(sketch, "E7.0.78.0", {"start": v(19.81, -2.54) * mm, "end": v(19.69, -2.32) * mm});
            skLineSegment(sketch, "E7.3.78.0", {"start": v(19.69, -2.32) * mm, "end": v(19.56, -2.54) * mm});
            skLineSegment(sketch, "E7.0.79.0", {"start": v(20.07, -2.54) * mm, "end": v(19.94, -2.32) * mm});
            skLineSegment(sketch, "E7.3.79.0", {"start": v(19.94, -2.32) * mm, "end": v(19.81, -2.54) * mm});
            skLineSegment(sketch, "E7.0.80.0", {"start": v(20.32, -2.54) * mm, "end": v(20.2, -2.32) * mm});
            skLineSegment(sketch, "E7.3.80.0", {"start": v(20.2, -2.32) * mm, "end": v(20.07, -2.54) * mm});
            skLineSegment(sketch, "E7.0.81.0", {"start": v(20.57, -2.54) * mm, "end": v(20.45, -2.32) * mm});
            skLineSegment(sketch, "E7.3.81.0", {"start": v(20.45, -2.32) * mm, "end": v(20.32, -2.54) * mm});
            skLineSegment(sketch, "E7.0.82.0", {"start": v(20.83, -2.54) * mm, "end": v(20.7, -2.32) * mm});
            skLineSegment(sketch, "E7.3.82.0", {"start": v(20.7, -2.32) * mm, "end": v(20.57, -2.54) * mm});
            skLineSegment(sketch, "E7.0.83.0", {"start": v(21.08, -2.54) * mm, "end": v(20.96, -2.32) * mm});
            skLineSegment(sketch, "E7.3.83.0", {"start": v(20.96, -2.32) * mm, "end": v(20.83, -2.54) * mm});
            skLineSegment(sketch, "E7.0.84.0", {"start": v(21.34, -2.54) * mm, "end": v(21.2, -2.32) * mm});
            skLineSegment(sketch, "E7.3.84.0", {"start": v(21.2, -2.32) * mm, "end": v(21.08, -2.54) * mm});
            skLineSegment(sketch, "E8.0.85.0", {"start": v(21.6, -2.54) * mm, "end": v(21.46, -2.32) * mm});
            skLineSegment(sketch, "E8.3.85.0", {"start": v(21.46, -2.32) * mm, "end": v(21.34, -2.54) * mm});
            skLineSegment(sketch, "E8.0.86.0", {"start": v(21.84, -2.54) * mm, "end": v(21.72, -2.32) * mm});
            skLineSegment(sketch, "E8.3.86.0", {"start": v(21.72, -2.32) * mm, "end": v(21.6, -2.54) * mm});
            skLineSegment(sketch, "E8.0.87.0", {"start": v(22.1, -2.54) * mm, "end": v(21.97, -2.32) * mm});
            skLineSegment(sketch, "E8.3.87.0", {"start": v(21.97, -2.32) * mm, "end": v(21.84, -2.54) * mm});
            skLineSegment(sketch, "E8.0.88.0", {"start": v(22.35, -2.54) * mm, "end": v(22.23, -2.32) * mm});
            skLineSegment(sketch, "E8.3.88.0", {"start": v(22.23, -2.32) * mm, "end": v(22.1, -2.54) * mm});
            skLineSegment(sketch, "E8.0.89.0", {"start": v(22.6, -2.54) * mm, "end": v(22.48, -2.32) * mm});
            skLineSegment(sketch, "E8.3.89.0", {"start": v(22.48, -2.32) * mm, "end": v(22.35, -2.54) * mm});
            skLineSegment(sketch, "E8.0.90.0", {"start": v(22.86, -2.54) * mm, "end": v(22.73, -2.32) * mm});
            skLineSegment(sketch, "E8.3.90.0", {"start": v(22.73, -2.32) * mm, "end": v(22.6, -2.54) * mm});
            skLineSegment(sketch, "E8.0.91.0", {"start": v(23.11, -2.54) * mm, "end": v(22.99, -2.32) * mm});
            skLineSegment(sketch, "E8.3.91.0", {"start": v(22.99, -2.32) * mm, "end": v(22.86, -2.54) * mm});
            skLineSegment(sketch, "E8.0.92.0", {"start": v(23.37, -2.54) * mm, "end": v(23.24, -2.32) * mm});
            skLineSegment(sketch, "E8.3.92.0", {"start": v(23.24, -2.32) * mm, "end": v(23.11, -2.54) * mm});
            skLineSegment(sketch, "E8.0.93.0", {"start": v(23.62, -2.54) * mm, "end": v(23.5, -2.32) * mm});
            skLineSegment(sketch, "E8.3.93.0", {"start": v(23.5, -2.32) * mm, "end": v(23.37, -2.54) * mm});
            skLineSegment(sketch, "E8.0.94.0", {"start": v(23.88, -2.54) * mm, "end": v(23.75, -2.32) * mm});
            skLineSegment(sketch, "E8.3.94.0", {"start": v(23.75, -2.32) * mm, "end": v(23.62, -2.54) * mm});
            skLineSegment(sketch, "E8.0.95.0", {"start": v(24.13, -2.54) * mm, "end": v(24, -2.32) * mm});
            skLineSegment(sketch, "E8.3.95.0", {"start": v(24, -2.32) * mm, "end": v(23.88, -2.54) * mm});
            skLineSegment(sketch, "E8.0.96.0", {"start": v(24.38, -2.54) * mm, "end": v(24.26, -2.32) * mm});
            skLineSegment(sketch, "E8.3.96.0", {"start": v(24.26, -2.32) * mm, "end": v(24.13, -2.54) * mm});
            skLineSegment(sketch, "E8.0.97.0", {"start": v(24.64, -2.54) * mm, "end": v(24.51, -2.32) * mm});
            skLineSegment(sketch, "E8.3.97.0", {"start": v(24.51, -2.32) * mm, "end": v(24.38, -2.54) * mm});
            skLineSegment(sketch, "E8.0.98.0", {"start": v(24.9, -2.54) * mm, "end": v(24.77, -2.32) * mm});
            skLineSegment(sketch, "E8.3.98.0", {"start": v(24.77, -2.32) * mm, "end": v(24.64, -2.54) * mm});
            skLineSegment(sketch, "E9.0.76.0", {"start": v(-19.3, -2.54) * mm, "end": v(-19.43, -2.32) * mm});
            skLineSegment(sketch, "E9.3.76.0", {"start": v(-19.43, -2.32) * mm, "end": v(-19.56, -2.54) * mm});
            skLineSegment(sketch, "E9.0.77.0", {"start": v(-19.56, -2.54) * mm, "end": v(-19.68, -2.32) * mm});
            skLineSegment(sketch, "E9.3.77.0", {"start": v(-19.68, -2.32) * mm, "end": v(-19.81, -2.54) * mm});
            skLineSegment(sketch, "E9.0.78.0", {"start": v(-19.81, -2.54) * mm, "end": v(-19.94, -2.32) * mm});
            skLineSegment(sketch, "E9.3.78.0", {"start": v(-19.94, -2.32) * mm, "end": v(-20.07, -2.54) * mm});
            skLineSegment(sketch, "E9.0.79.0", {"start": v(-20.07, -2.54) * mm, "end": v(-20.2, -2.32) * mm});
            skLineSegment(sketch, "E9.3.79.0", {"start": v(-20.2, -2.32) * mm, "end": v(-20.32, -2.54) * mm});
            skLineSegment(sketch, "E9.0.80.0", {"start": v(-20.32, -2.54) * mm, "end": v(-20.45, -2.32) * mm});
            skLineSegment(sketch, "E9.3.80.0", {"start": v(-20.45, -2.32) * mm, "end": v(-20.57, -2.54) * mm});
            skLineSegment(sketch, "E9.0.81.0", {"start": v(-20.57, -2.54) * mm, "end": v(-20.7, -2.32) * mm});
            skLineSegment(sketch, "E9.3.81.0", {"start": v(-20.7, -2.32) * mm, "end": v(-20.83, -2.54) * mm});
            skLineSegment(sketch, "E9.0.82.0", {"start": v(-20.83, -2.54) * mm, "end": v(-20.95, -2.32) * mm});
            skLineSegment(sketch, "E9.3.82.0", {"start": v(-20.95, -2.32) * mm, "end": v(-21.08, -2.54) * mm});
            skLineSegment(sketch, "E9.0.83.0", {"start": v(-21.08, -2.54) * mm, "end": v(-21.2, -2.32) * mm});
            skLineSegment(sketch, "E9.3.83.0", {"start": v(-21.2, -2.32) * mm, "end": v(-21.34, -2.54) * mm});
            skLineSegment(sketch, "E9.0.84.0", {"start": v(-21.34, -2.54) * mm, "end": v(-21.46, -2.32) * mm});
            skLineSegment(sketch, "E9.3.84.0", {"start": v(-21.46, -2.32) * mm, "end": v(-21.59, -2.54) * mm});
            skLineSegment(sketch, "E9.0.85.0", {"start": v(-21.59, -2.54) * mm, "end": v(-21.72, -2.32) * mm});
            skLineSegment(sketch, "E9.3.85.0", {"start": v(-21.72, -2.32) * mm, "end": v(-21.84, -2.54) * mm});
            skLineSegment(sketch, "E9.0.86.0", {"start": v(-21.84, -2.54) * mm, "end": v(-21.97, -2.32) * mm});
            skLineSegment(sketch, "E9.3.86.0", {"start": v(-21.97, -2.32) * mm, "end": v(-22.1, -2.54) * mm});
            skLineSegment(sketch, "E9.0.87.0", {"start": v(-22.1, -2.54) * mm, "end": v(-22.22, -2.32) * mm});
            skLineSegment(sketch, "E9.3.87.0", {"start": v(-22.22, -2.32) * mm, "end": v(-22.35, -2.54) * mm});
            skLineSegment(sketch, "E9.0.88.0", {"start": v(-22.35, -2.54) * mm, "end": v(-22.48, -2.32) * mm});
            skLineSegment(sketch, "E9.3.88.0", {"start": v(-22.48, -2.32) * mm, "end": v(-22.6, -2.54) * mm});
            skLineSegment(sketch, "E9.0.89.0", {"start": v(-22.6, -2.54) * mm, "end": v(-22.73, -2.32) * mm});
            skLineSegment(sketch, "E9.3.89.0", {"start": v(-22.73, -2.32) * mm, "end": v(-22.86, -2.54) * mm});
            skLineSegment(sketch, "E9.0.90.0", {"start": v(-22.86, -2.54) * mm, "end": v(-22.99, -2.32) * mm});
            skLineSegment(sketch, "E9.3.90.0", {"start": v(-22.99, -2.32) * mm, "end": v(-23.11, -2.54) * mm});
            skLineSegment(sketch, "E9.0.91.0", {"start": v(-23.11, -2.54) * mm, "end": v(-23.24, -2.32) * mm});
            skLineSegment(sketch, "E9.3.91.0", {"start": v(-23.24, -2.32) * mm, "end": v(-23.37, -2.54) * mm});
            skLineSegment(sketch, "E9.0.92.0", {"start": v(-23.37, -2.54) * mm, "end": v(-23.5, -2.32) * mm});
            skLineSegment(sketch, "E9.3.92.0", {"start": v(-23.5, -2.32) * mm, "end": v(-23.62, -2.54) * mm});
            skLineSegment(sketch, "E9.0.93.0", {"start": v(-23.62, -2.54) * mm, "end": v(-23.75, -2.32) * mm});
            skLineSegment(sketch, "E9.3.93.0", {"start": v(-23.75, -2.32) * mm, "end": v(-23.88, -2.54) * mm});
            skLineSegment(sketch, "E9.0.94.0", {"start": v(-23.88, -2.54) * mm, "end": v(-24, -2.32) * mm});
            skLineSegment(sketch, "E9.3.94.0", {"start": v(-24, -2.32) * mm, "end": v(-24.13, -2.54) * mm});
            skLineSegment(sketch, "E9.0.95.0", {"start": v(-24.13, -2.54) * mm, "end": v(-24.26, -2.32) * mm});
            skLineSegment(sketch, "E9.3.95.0", {"start": v(-24.26, -2.32) * mm, "end": v(-24.38, -2.54) * mm});
            skLineSegment(sketch, "E9.0.96.0", {"start": v(-24.38, -2.54) * mm, "end": v(-24.51, -2.32) * mm});
            skLineSegment(sketch, "E9.3.96.0", {"start": v(-24.51, -2.32) * mm, "end": v(-24.64, -2.54) * mm});
            skLineSegment(sketch, "E9.0.97.0", {"start": v(-24.64, -2.54) * mm, "end": v(-24.76, -2.32) * mm});
            skLineSegment(sketch, "E9.3.97.0", {"start": v(-24.76, -2.32) * mm, "end": v(-24.9, -2.54) * mm});
            skLineSegment(sketch, "E10", {"start": v(-24.9, -2.54) * mm, "end": v(-24.9, -2.8) * mm});
            skLineSegment(sketch, "E11", {"start": v(-24.9, -2.8) * mm, "end": v(24.9, -2.8) * mm});
            skLineSegment(sketch, "E12", {"start": v(24.9, -2.8) * mm, "end": v(24.9, -2.54) * mm});
            skLineSegment(sketch, "E13.MirrorCS", {"start": v(7.5, 2.32) * mm, "end": v(7.37, 2.54) * mm});
            skLineSegment(sketch, "E14.MirrorCS", {"start": v(-0.5, 2.54) * mm, "end": v(-0.63, 2.32) * mm});
            skLineSegment(sketch, "E15.MirrorCS", {"start": v(-1.4, 2.32) * mm, "end": v(-1.52, 2.54) * mm});
            skLineSegment(sketch, "E16.MirrorCS", {"start": v(7.24, 2.32) * mm, "end": v(7.11, 2.54) * mm});
            skLineSegment(sketch, "E17.MirrorCS", {"start": v(-16.5, 2.54) * mm, "end": v(-16.64, 2.32) * mm});
            skLineSegment(sketch, "E18.MirrorCS", {"start": v(-20.83, 2.54) * mm, "end": v(-20.95, 2.32) * mm});
            skLineSegment(sketch, "E19.MirrorCS", {"start": v(20.57, 2.54) * mm, "end": v(20.45, 2.32) * mm});
            skLineSegment(sketch, "E20.MirrorCS", {"start": v(2.54, 2.54) * mm, "end": v(2.41, 2.32) * mm});
            skLineSegment(sketch, "E21.MirrorCS", {"start": v(-22.86, 2.54) * mm, "end": v(-22.99, 2.32) * mm});
            skLineSegment(sketch, "E22.MirrorCS", {"start": v(0, 2.54) * mm, "end": v(-0.13, 2.32) * mm});
            skLineSegment(sketch, "E23.MirrorCS", {"start": v(-0.25, 2.54) * mm, "end": v(-0.38, 2.32) * mm});
            skLineSegment(sketch, "E24.MirrorCS", {"start": v(-16.76, 2.54) * mm, "end": v(-16.9, 2.32) * mm});
            skLineSegment(sketch, "E25.MirrorCS", {"start": v(2.67, 2.32) * mm, "end": v(2.54, 2.54) * mm});
            skLineSegment(sketch, "E26.MirrorCS", {"start": v(-6.35, 2.54) * mm, "end": v(-6.48, 2.32) * mm});
            skLineSegment(sketch, "E27.MirrorCS", {"start": v(7.62, 2.54) * mm, "end": v(7.5, 2.32) * mm});
            skLineSegment(sketch, "E28.MirrorCS", {"start": v(-0.25, 2.54) * mm, "end": v(0, 2.54) * mm, "construction": true});
            skLineSegment(sketch, "E29.MirrorCS", {"start": v(-0.25, 2.54) * mm, "end": v(-0.5, 2.54) * mm, "construction": true});
            skLineSegment(sketch, "E30.MirrorCS", {"start": v(13.72, 2.54) * mm, "end": v(13.59, 2.32) * mm});
            skLineSegment(sketch, "E31.MirrorCS", {"start": v(-11.56, 2.32) * mm, "end": v(-11.68, 2.54) * mm});
            skLineSegment(sketch, "E32.MirrorCS", {"start": v(-12.45, 2.54) * mm, "end": v(-12.57, 2.32) * mm});
            skLineSegment(sketch, "E33.MirrorCS", {"start": v(8.64, 2.54) * mm, "end": v(8.5, 2.32) * mm});
            skLineSegment(sketch, "E34.MirrorCS", {"start": v(-4.95, 2.32) * mm, "end": v(-5.08, 2.54) * mm});
            skLineSegment(sketch, "E35.MirrorCS", {"start": v(-20.07, 2.54) * mm, "end": v(-20.2, 2.32) * mm});
            skLineSegment(sketch, "E36.MirrorCS", {"start": v(-1.78, 2.54) * mm, "end": v(-1.9, 2.32) * mm});
            skLineSegment(sketch, "E37.MirrorCS", {"start": v(11.56, 2.32) * mm, "end": v(11.43, 2.54) * mm});
            skLineSegment(sketch, "E38.MirrorCS", {"start": v(6.86, 2.54) * mm, "end": v(6.73, 2.32) * mm});
            skLineSegment(sketch, "E39.MirrorCS", {"start": v(-10.67, 2.54) * mm, "end": v(-10.8, 2.32) * mm});
            skLineSegment(sketch, "E40.MirrorCS", {"start": v(18.42, 2.32) * mm, "end": v(18.29, 2.54) * mm});
            skLineSegment(sketch, "E41.MirrorCS", {"start": v(-5.46, 2.32) * mm, "end": v(-5.59, 2.54) * mm});
            skLineSegment(sketch, "E42.MirrorCS", {"start": v(12.7, 2.54) * mm, "end": v(12.57, 2.32) * mm});
            skLineSegment(sketch, "E43.MirrorCS", {"start": v(17.78, 2.54) * mm, "end": v(17.65, 2.32) * mm});
            skLineSegment(sketch, "E44.MirrorCS", {"start": v(5.46, 2.32) * mm, "end": v(5.33, 2.54) * mm});
            skLineSegment(sketch, "E45.MirrorCS", {"start": v(16.76, 2.54) * mm, "end": v(16.64, 2.32) * mm});
            skLineSegment(sketch, "E46.MirrorCS", {"start": v(-4.32, 2.54) * mm, "end": v(-4.44, 2.32) * mm});
            skLineSegment(sketch, "E47.MirrorCS", {"start": v(-8.64, 2.54) * mm, "end": v(-8.76, 2.32) * mm});
            skLineSegment(sketch, "E48.MirrorCS", {"start": v(7.75, 2.32) * mm, "end": v(7.62, 2.54) * mm});
            skLineSegment(sketch, "E49.MirrorCS", {"start": v(8.9, 2.54) * mm, "end": v(8.76, 2.32) * mm});
            skLineSegment(sketch, "E50.MirrorCS", {"start": v(20.2, 2.32) * mm, "end": v(20.07, 2.54) * mm});
            skLineSegment(sketch, "E51.MirrorCS", {"start": v(2.41, 2.32) * mm, "end": v(2.29, 2.54) * mm});
            skLineSegment(sketch, "E52.MirrorCS", {"start": v(21.84, 2.54) * mm, "end": v(21.72, 2.32) * mm});
            skLineSegment(sketch, "E53.MirrorCS", {"start": v(-22.1, 2.54) * mm, "end": v(-22.22, 2.32) * mm});
            skLineSegment(sketch, "E54.MirrorCS", {"start": v(20.32, 2.54) * mm, "end": v(20.2, 2.32) * mm});
            skLineSegment(sketch, "E55.MirrorCS", {"start": v(-13.59, 2.32) * mm, "end": v(-13.72, 2.54) * mm});
            skLineSegment(sketch, "E56.MirrorCS", {"start": v(-20.95, 2.32) * mm, "end": v(-21.08, 2.54) * mm});
            skLineSegment(sketch, "E57.MirrorCS", {"start": v(14.73, 2.54) * mm, "end": v(14.6, 2.32) * mm});
            skLineSegment(sketch, "E58.MirrorCS", {"start": v(15.5, 2.54) * mm, "end": v(15.37, 2.32) * mm});
            skLineSegment(sketch, "E59.MirrorCS", {"start": v(4.83, 2.54) * mm, "end": v(4.7, 2.32) * mm});
            skLineSegment(sketch, "E60.MirrorCS", {"start": v(8.13, 2.54) * mm, "end": v(8, 2.32) * mm});
            skLineSegment(sketch, "E61.MirrorCS", {"start": v(-1.52, 2.54) * mm, "end": v(-1.65, 2.32) * mm});
            skLineSegment(sketch, "E62.MirrorCS", {"start": v(12.95, 2.54) * mm, "end": v(12.83, 2.32) * mm});
            skLineSegment(sketch, "E63.MirrorCS", {"start": v(-14.73, 2.54) * mm, "end": v(-14.86, 2.32) * mm});
            skLineSegment(sketch, "E64.MirrorCS", {"start": v(-9.52, 2.32) * mm, "end": v(-9.65, 2.54) * mm});
            skLineSegment(sketch, "E65.MirrorCS", {"start": v(-17.14, 2.32) * mm, "end": v(-17.27, 2.54) * mm});
            skLineSegment(sketch, "E66.MirrorCS", {"start": v(-2.54, 2.54) * mm, "end": v(-2.67, 2.32) * mm});
            skLineSegment(sketch, "E67.MirrorCS", {"start": v(-21.2, 2.32) * mm, "end": v(-21.34, 2.54) * mm});
            skLineSegment(sketch, "E68.MirrorCS", {"start": v(17.02, 2.54) * mm, "end": v(16.9, 2.32) * mm});
            skLineSegment(sketch, "E69.MirrorCS", {"start": v(18.8, 2.54) * mm, "end": v(18.67, 2.32) * mm});
            skLineSegment(sketch, "E70.MirrorCS", {"start": v(22.6, 2.54) * mm, "end": v(22.48, 2.32) * mm});
            skLineSegment(sketch, "E71.MirrorCS", {"start": v(-24.13, 2.54) * mm, "end": v(-24.26, 2.32) * mm});
            skLineSegment(sketch, "E72.MirrorCS", {"start": v(-1.27, 2.54) * mm, "end": v(-1.4, 2.32) * mm});
            skLineSegment(sketch, "E73.MirrorCS", {"start": v(-16.38, 2.32) * mm, "end": v(-16.5, 2.54) * mm});
            skLineSegment(sketch, "E74.MirrorCS", {"start": v(-12.7, 2.54) * mm, "end": v(-12.83, 2.32) * mm});
            skLineSegment(sketch, "E75.MirrorCS", {"start": v(-18.8, 2.54) * mm, "end": v(-18.92, 2.32) * mm});
            skLineSegment(sketch, "E76.MirrorCS", {"start": v(-16.9, 2.32) * mm, "end": v(-17.02, 2.54) * mm});
            skLineSegment(sketch, "E77.MirrorCS", {"start": v(-22.6, 2.54) * mm, "end": v(-22.73, 2.32) * mm});
            skLineSegment(sketch, "E78.MirrorCS", {"start": v(0.13, 2.32) * mm, "end": v(0, 2.54) * mm});
            skLineSegment(sketch, "E79.MirrorCS", {"start": v(-1.14, 2.32) * mm, "end": v(-1.27, 2.54) * mm});
            skLineSegment(sketch, "E80.MirrorCS", {"start": v(-20.7, 2.32) * mm, "end": v(-20.83, 2.54) * mm});
            skLineSegment(sketch, "E81.MirrorCS", {"start": v(-1.65, 2.32) * mm, "end": v(-1.78, 2.54) * mm});
            skLineSegment(sketch, "E82.MirrorCS", {"start": v(-2.92, 2.32) * mm, "end": v(-3.05, 2.54) * mm});
            skLineSegment(sketch, "E83.MirrorCS", {"start": v(7.11, 2.54) * mm, "end": v(6.99, 2.32) * mm});
            skLineSegment(sketch, "E84.MirrorCS", {"start": v(-22.73, 2.32) * mm, "end": v(-22.86, 2.54) * mm});
            skLineSegment(sketch, "E85.MirrorCS", {"start": v(-21.08, 2.54) * mm, "end": v(-21.2, 2.32) * mm});
            skLineSegment(sketch, "E86.MirrorCS", {"start": v(-0.13, 2.32) * mm, "end": v(-0.25, 2.54) * mm});
            skLineSegment(sketch, "E87.MirrorCS", {"start": v(-22.99, 2.32) * mm, "end": v(-23.11, 2.54) * mm});
            skLineSegment(sketch, "E88.MirrorCS", {"start": v(16.38, 2.32) * mm, "end": v(16.26, 2.54) * mm});
            skLineSegment(sketch, "E89.MirrorCS", {"start": v(-20.57, 2.54) * mm, "end": v(-20.7, 2.32) * mm});
            skLineSegment(sketch, "E90.MirrorCS", {"start": v(-10.41, 2.54) * mm, "end": v(-10.54, 2.32) * mm});
            skLineSegment(sketch, "E91.MirrorCS", {"start": v(-21.59, 2.54) * mm, "end": v(-21.72, 2.32) * mm});
            skLineSegment(sketch, "E92.MirrorCS", {"start": v(2.8, 2.54) * mm, "end": v(2.67, 2.32) * mm});
            skLineSegment(sketch, "E93.MirrorCS", {"start": v(3.43, 2.32) * mm, "end": v(3.3, 2.54) * mm});
            skLineSegment(sketch, "E94.MirrorCS", {"start": v(9.27, 2.32) * mm, "end": v(9.14, 2.54) * mm});
            skLineSegment(sketch, "E95.MirrorCS", {"start": v(-7.5, 2.32) * mm, "end": v(-7.62, 2.54) * mm});
            skLineSegment(sketch, "E96.MirrorCS", {"start": v(2.29, 2.54) * mm, "end": v(2.16, 2.32) * mm});
            skLineSegment(sketch, "E97.MirrorCS", {"start": v(-0.63, 2.32) * mm, "end": v(-0.76, 2.54) * mm});
            skLineSegment(sketch, "E98.MirrorCS", {"start": v(-20.45, 2.32) * mm, "end": v(-20.57, 2.54) * mm});
            skLineSegment(sketch, "E99.MirrorCS", {"start": v(-0.38, 2.32) * mm, "end": v(-0.5, 2.54) * mm});
            skLineSegment(sketch, "E100.MirrorCS", {"start": v(-22.48, 2.32) * mm, "end": v(-22.6, 2.54) * mm});
            skLineSegment(sketch, "E101.MirrorCS", {"start": v(10.67, 2.54) * mm, "end": v(10.54, 2.32) * mm});
            skLineSegment(sketch, "E102.MirrorCS", {"start": v(-16.64, 2.32) * mm, "end": v(-16.76, 2.54) * mm});
            skLineSegment(sketch, "E103.MirrorCS", {"start": v(-14.48, 2.54) * mm, "end": v(-14.6, 2.32) * mm});
            skLineSegment(sketch, "E104.MirrorCS", {"start": v(-23.11, 2.54) * mm, "end": v(-23.24, 2.32) * mm});
            skLineSegment(sketch, "E105.MirrorCS", {"start": v(20.83, 2.54) * mm, "end": v(20.7, 2.32) * mm});
            skLineSegment(sketch, "E106.MirrorCS", {"start": v(-2.29, 2.54) * mm, "end": v(-2.41, 2.32) * mm});
            skLineSegment(sketch, "E107.MirrorCS", {"start": v(20.7, 2.32) * mm, "end": v(20.57, 2.54) * mm});
            skLineSegment(sketch, "E108.MirrorCS", {"start": v(20.45, 2.32) * mm, "end": v(20.32, 2.54) * mm});
            skLineSegment(sketch, "E109.MirrorCS", {"start": v(6.6, 2.54) * mm, "end": v(6.48, 2.32) * mm});
            skLineSegment(sketch, "E110.MirrorCS", {"start": v(-3.43, 2.32) * mm, "end": v(-3.56, 2.54) * mm});
            skLineSegment(sketch, "E111.MirrorCS", {"start": v(-4.57, 2.54) * mm, "end": v(-4.7, 2.32) * mm});
            skLineSegment(sketch, "E112.MirrorCS", {"start": v(7.87, 2.54) * mm, "end": v(7.75, 2.32) * mm});
            skLineSegment(sketch, "E113.MirrorCS", {"start": v(11.3, 2.32) * mm, "end": v(11.18, 2.54) * mm});
            skLineSegment(sketch, "E114.MirrorCS", {"start": v(-1.9, 2.32) * mm, "end": v(-2.03, 2.54) * mm});
            skLineSegment(sketch, "E115.MirrorCS", {"start": v(5.2, 2.32) * mm, "end": v(5.08, 2.54) * mm});
            skLineSegment(sketch, "E116.MirrorCS", {"start": v(-23.24, 2.32) * mm, "end": v(-23.37, 2.54) * mm});
            skLineSegment(sketch, "E117.MirrorCS", {"start": v(-15.62, 2.32) * mm, "end": v(-15.75, 2.54) * mm});
            skLineSegment(sketch, "E118.MirrorCS", {"start": v(7.37, 2.54) * mm, "end": v(7.24, 2.32) * mm});
            skLineSegment(sketch, "E119.MirrorCS", {"start": v(17.53, 2.54) * mm, "end": v(17.4, 2.32) * mm});
            skLineSegment(sketch, "E120.MirrorCS", {"start": v(-8.38, 2.54) * mm, "end": v(-8.5, 2.32) * mm});
            skLineSegment(sketch, "E121.MirrorCS", {"start": v(-17.02, 2.54) * mm, "end": v(-17.14, 2.32) * mm});
            skLineSegment(sketch, "E122.MirrorCS", {"start": v(-23.88, 2.54) * mm, "end": v(-24, 2.32) * mm});
            skLineSegment(sketch, "E123.MirrorCS", {"start": v(-4.44, 2.32) * mm, "end": v(-4.57, 2.54) * mm});
            skLineSegment(sketch, "E124.MirrorCS", {"start": v(4.95, 2.32) * mm, "end": v(4.83, 2.54) * mm});
            skLineSegment(sketch, "E125.MirrorCS", {"start": v(-18.16, 2.32) * mm, "end": v(-18.29, 2.54) * mm});
            skLineSegment(sketch, "E126.MirrorCS", {"start": v(8.38, 2.54) * mm, "end": v(8.26, 2.32) * mm});
            skLineSegment(sketch, "E127.MirrorCS", {"start": v(16.51, 2.54) * mm, "end": v(16.38, 2.32) * mm});
            skLineSegment(sketch, "E128.MirrorCS", {"start": v(-15.11, 2.32) * mm, "end": v(-15.24, 2.54) * mm});
            skLineSegment(sketch, "E129.MirrorCS", {"start": v(22.99, 2.32) * mm, "end": v(22.86, 2.54) * mm});
            skLineSegment(sketch, "E130.MirrorCS", {"start": v(-16, 2.54) * mm, "end": v(-16.13, 2.32) * mm});
            skLineSegment(sketch, "E131.MirrorCS", {"start": v(4.45, 2.32) * mm, "end": v(4.32, 2.54) * mm});
            skLineSegment(sketch, "E132.MirrorCS", {"start": v(9.02, 2.32) * mm, "end": v(8.9, 2.54) * mm});
            skLineSegment(sketch, "E133.MirrorCS", {"start": v(-17.9, 2.32) * mm, "end": v(-18.03, 2.54) * mm});
            skLineSegment(sketch, "E134.MirrorCS", {"start": v(15.62, 2.32) * mm, "end": v(15.5, 2.54) * mm});
            skLineSegment(sketch, "E135.MirrorCS", {"start": v(16.64, 2.32) * mm, "end": v(16.51, 2.54) * mm});
            skLineSegment(sketch, "E136.MirrorCS", {"start": v(24, 2.32) * mm, "end": v(23.88, 2.54) * mm});
            skLineSegment(sketch, "E137.MirrorCS", {"start": v(-19.81, 2.54) * mm, "end": v(-19.94, 2.32) * mm});
            skLineSegment(sketch, "E138.MirrorCS", {"start": v(-11.43, 2.54) * mm, "end": v(-11.56, 2.32) * mm});
            skLineSegment(sketch, "E139.MirrorCS", {"start": v(-18.03, 2.54) * mm, "end": v(-18.16, 2.32) * mm});
            skLineSegment(sketch, "E140.MirrorCS", {"start": v(-8.13, 2.54) * mm, "end": v(-8.25, 2.32) * mm});
            skLineSegment(sketch, "E141.MirrorCS", {"start": v(0.25, 2.54) * mm, "end": v(0.13, 2.32) * mm});
            skLineSegment(sketch, "E142.MirrorCS", {"start": v(17.15, 2.32) * mm, "end": v(17.02, 2.54) * mm});
            skLineSegment(sketch, "E143.MirrorCS", {"start": v(-16.13, 2.32) * mm, "end": v(-16.26, 2.54) * mm});
            skLineSegment(sketch, "E144.MirrorCS", {"start": v(-13.72, 2.54) * mm, "end": v(-13.84, 2.32) * mm});
            skLineSegment(sketch, "E145.MirrorCS", {"start": v(23.11, 2.54) * mm, "end": v(22.99, 2.32) * mm});
            skLineSegment(sketch, "E146.MirrorCS", {"start": v(4.06, 2.54) * mm, "end": v(3.94, 2.32) * mm});
            skLineSegment(sketch, "E147.MirrorCS", {"start": v(16, 2.54) * mm, "end": v(15.88, 2.32) * mm});
            skLineSegment(sketch, "E148.MirrorCS", {"start": v(8.26, 2.32) * mm, "end": v(8.13, 2.54) * mm});
            skLineSegment(sketch, "E149.MirrorCS", {"start": v(-23.37, 2.54) * mm, "end": v(-23.5, 2.32) * mm});
            skLineSegment(sketch, "E150.MirrorCS", {"start": v(14.22, 2.54) * mm, "end": v(14.1, 2.32) * mm});
            skLineSegment(sketch, "E151.MirrorCS", {"start": v(3.05, 2.54) * mm, "end": v(2.92, 2.32) * mm});
            skLineSegment(sketch, "E152.MirrorCS", {"start": v(-2.8, 2.54) * mm, "end": v(-2.92, 2.32) * mm});
            skLineSegment(sketch, "E153.MirrorCS", {"start": v(-8.76, 2.32) * mm, "end": v(-8.89, 2.54) * mm});
            skLineSegment(sketch, "E154.MirrorCS", {"start": v(11.18, 2.54) * mm, "end": v(11.05, 2.32) * mm});
            skLineSegment(sketch, "E155.MirrorCS", {"start": v(20.07, 2.54) * mm, "end": v(19.94, 2.32) * mm});
            skLineSegment(sketch, "E156.MirrorCS", {"start": v(11.05, 2.32) * mm, "end": v(10.92, 2.54) * mm});
            skLineSegment(sketch, "E157.MirrorCS", {"start": v(6.73, 2.32) * mm, "end": v(6.6, 2.54) * mm});
            skLineSegment(sketch, "E158.MirrorCS", {"start": v(-17.27, 2.54) * mm, "end": v(-17.4, 2.32) * mm});
            skLineSegment(sketch, "E159.MirrorCS", {"start": v(-14.22, 2.54) * mm, "end": v(-14.35, 2.32) * mm});
            skLineSegment(sketch, "E160.MirrorCS", {"start": v(12.83, 2.32) * mm, "end": v(12.7, 2.54) * mm});
            skLineSegment(sketch, "E161.MirrorCS", {"start": v(21.97, 2.32) * mm, "end": v(21.84, 2.54) * mm});
            skLineSegment(sketch, "E162.MirrorCS", {"start": v(16.13, 2.32) * mm, "end": v(16, 2.54) * mm});
            skLineSegment(sketch, "E163.MirrorCS", {"start": v(-2.41, 2.32) * mm, "end": v(-2.54, 2.54) * mm});
            skLineSegment(sketch, "E164.MirrorCS", {"start": v(4.7, 2.32) * mm, "end": v(4.57, 2.54) * mm});
            skLineSegment(sketch, "E165.MirrorCS", {"start": v(14.48, 2.54) * mm, "end": v(14.35, 2.32) * mm});
            skLineSegment(sketch, "E166.MirrorCS", {"start": v(5.84, 2.54) * mm, "end": v(5.72, 2.32) * mm});
            skLineSegment(sketch, "E167.MirrorCS", {"start": v(-21.84, 2.54) * mm, "end": v(-21.97, 2.32) * mm});
            skLineSegment(sketch, "E168.MirrorCS", {"start": v(-11.94, 2.54) * mm, "end": v(-12.06, 2.32) * mm});
            skLineSegment(sketch, "E169.MirrorCS", {"start": v(-18.92, 2.32) * mm, "end": v(-19.05, 2.54) * mm});
            skLineSegment(sketch, "E170.MirrorCS", {"start": v(15.88, 2.32) * mm, "end": v(15.75, 2.54) * mm});
            skLineSegment(sketch, "E171.MirrorCS", {"start": v(10.54, 2.32) * mm, "end": v(10.41, 2.54) * mm});
            skLineSegment(sketch, "E172.MirrorCS", {"start": v(-11.68, 2.54) * mm, "end": v(-11.81, 2.32) * mm});
            skLineSegment(sketch, "E173.MirrorCS", {"start": v(10.8, 2.32) * mm, "end": v(10.67, 2.54) * mm});
            skLineSegment(sketch, "E174.MirrorCS", {"start": v(1.65, 2.32) * mm, "end": v(1.52, 2.54) * mm});
            skLineSegment(sketch, "E175.MirrorCS", {"start": v(-9.27, 2.32) * mm, "end": v(-9.4, 2.54) * mm});
            skLineSegment(sketch, "E176.MirrorCS", {"start": v(14.35, 2.32) * mm, "end": v(14.22, 2.54) * mm});
            skLineSegment(sketch, "E177.MirrorCS", {"start": v(-24.51, 2.32) * mm, "end": v(-24.64, 2.54) * mm});
            skLineSegment(sketch, "E178.MirrorCS", {"start": v(18.67, 2.32) * mm, "end": v(18.54, 2.54) * mm});
            skLineSegment(sketch, "E179.MirrorCS", {"start": v(-12.83, 2.32) * mm, "end": v(-12.95, 2.54) * mm});
            skLineSegment(sketch, "E180.MirrorCS", {"start": v(8, 2.32) * mm, "end": v(7.87, 2.54) * mm});
            skLineSegment(sketch, "E181.MirrorCS", {"start": v(-9.65, 2.54) * mm, "end": v(-9.78, 2.32) * mm});
            skLineSegment(sketch, "E182.MirrorCS", {"start": v(-8, 2.32) * mm, "end": v(-8.13, 2.54) * mm});
            skLineSegment(sketch, "E183.MirrorCS", {"start": v(6.35, 2.54) * mm, "end": v(6.22, 2.32) * mm});
            skLineSegment(sketch, "E184.MirrorCS", {"start": v(8.5, 2.32) * mm, "end": v(8.38, 2.54) * mm});
            skLineSegment(sketch, "E185.MirrorCS", {"start": v(-19.94, 2.32) * mm, "end": v(-20.07, 2.54) * mm});
            skLineSegment(sketch, "E186.MirrorCS", {"start": v(5.33, 2.54) * mm, "end": v(5.2, 2.32) * mm});
            skLineSegment(sketch, "E187.MirrorCS", {"start": v(-11.81, 2.32) * mm, "end": v(-11.94, 2.54) * mm});
            skLineSegment(sketch, "E188.MirrorCS", {"start": v(-12.2, 2.54) * mm, "end": v(-12.32, 2.32) * mm});
            skLineSegment(sketch, "E189.MirrorCS", {"start": v(11.68, 2.54) * mm, "end": v(11.56, 2.32) * mm});
            skLineSegment(sketch, "E190.MirrorCS", {"start": v(-21.34, 2.54) * mm, "end": v(-21.46, 2.32) * mm});
            skLineSegment(sketch, "E191.MirrorCS", {"start": v(-10.54, 2.32) * mm, "end": v(-10.67, 2.54) * mm});
            skLineSegment(sketch, "E192.MirrorCS", {"start": v(-14.86, 2.32) * mm, "end": v(-14.99, 2.54) * mm});
            skLineSegment(sketch, "E193.MirrorCS", {"start": v(-21.46, 2.32) * mm, "end": v(-21.59, 2.54) * mm});
            skLineSegment(sketch, "E194.MirrorCS", {"start": v(18.16, 2.32) * mm, "end": v(18.03, 2.54) * mm});
            skLineSegment(sketch, "E195.MirrorCS", {"start": v(14.6, 2.32) * mm, "end": v(14.48, 2.54) * mm});
            skLineSegment(sketch, "E196.MirrorCS", {"start": v(18.92, 2.32) * mm, "end": v(18.8, 2.54) * mm});
            skLineSegment(sketch, "E197.MirrorCS", {"start": v(-4.2, 2.32) * mm, "end": v(-4.32, 2.54) * mm});
            skLineSegment(sketch, "E198.MirrorCS", {"start": v(18.03, 2.54) * mm, "end": v(17.9, 2.32) * mm});
            skLineSegment(sketch, "E199.MirrorCS", {"start": v(12.57, 2.32) * mm, "end": v(12.45, 2.54) * mm});
            skLineSegment(sketch, "E200.MirrorCS", {"start": v(13.97, 2.54) * mm, "end": v(13.84, 2.32) * mm});
            skLineSegment(sketch, "E201.MirrorCS", {"start": v(9.78, 2.32) * mm, "end": v(9.65, 2.54) * mm});
            skLineSegment(sketch, "E202.MirrorCS", {"start": v(-6.22, 2.32) * mm, "end": v(-6.35, 2.54) * mm});
            skLineSegment(sketch, "E203.MirrorCS", {"start": v(-17.53, 2.54) * mm, "end": v(-17.65, 2.32) * mm});
            skLineSegment(sketch, "E204.MirrorCS", {"start": v(10.92, 2.54) * mm, "end": v(10.8, 2.32) * mm});
            skLineSegment(sketch, "E205.MirrorCS", {"start": v(12.45, 2.54) * mm, "end": v(12.32, 2.32) * mm});
            skLineSegment(sketch, "E206.MirrorCS", {"start": v(21.6, 2.54) * mm, "end": v(21.46, 2.32) * mm});
            skLineSegment(sketch, "E207.MirrorCS", {"start": v(-6.73, 2.32) * mm, "end": v(-6.86, 2.54) * mm});
            skLineSegment(sketch, "E208.MirrorCS", {"start": v(-9.9, 2.54) * mm, "end": v(-10.03, 2.32) * mm});
            skLineSegment(sketch, "E209.MirrorCS", {"start": v(-18.41, 2.32) * mm, "end": v(-18.54, 2.54) * mm});
            skLineSegment(sketch, "E210.MirrorCS", {"start": v(-6.6, 2.54) * mm, "end": v(-6.73, 2.32) * mm});
            skLineSegment(sketch, "E211.MirrorCS", {"start": v(-13.97, 2.54) * mm, "end": v(-14.1, 2.32) * mm});
            skLineSegment(sketch, "E212.MirrorCS", {"start": v(15.11, 2.32) * mm, "end": v(14.99, 2.54) * mm});
            skLineSegment(sketch, "E213.MirrorCS", {"start": v(-7.87, 2.54) * mm, "end": v(-8, 2.32) * mm});
            skLineSegment(sketch, "E214.MirrorCS", {"start": v(-3.8, 2.54) * mm, "end": v(-3.94, 2.32) * mm});
            skLineSegment(sketch, "E215.MirrorCS", {"start": v(-11.05, 2.32) * mm, "end": v(-11.18, 2.54) * mm});
            skLineSegment(sketch, "E216.MirrorCS", {"start": v(19.3, 2.54) * mm, "end": v(19.18, 2.32) * mm});
            skLineSegment(sketch, "E217.MirrorCS", {"start": v(-3.94, 2.32) * mm, "end": v(-4.06, 2.54) * mm});
            skLineSegment(sketch, "E218.MirrorCS", {"start": v(3.3, 2.54) * mm, "end": v(3.18, 2.32) * mm});
            skLineSegment(sketch, "E219.MirrorCS", {"start": v(17.4, 2.32) * mm, "end": v(17.27, 2.54) * mm});
            skLineSegment(sketch, "E220.MirrorCS", {"start": v(-19.3, 2.54) * mm, "end": v(-19.43, 2.32) * mm});
            skLineSegment(sketch, "E221.MirrorCS", {"start": v(15.37, 2.32) * mm, "end": v(15.24, 2.54) * mm});
            skLineSegment(sketch, "E222.MirrorCS", {"start": v(13.08, 2.32) * mm, "end": v(12.95, 2.54) * mm});
            skLineSegment(sketch, "E223.MirrorCS", {"start": v(-23.62, 2.54) * mm, "end": v(-23.75, 2.32) * mm});
            skLineSegment(sketch, "E224.MirrorCS", {"start": v(-7.24, 2.32) * mm, "end": v(-7.37, 2.54) * mm});
            skLineSegment(sketch, "E225.MirrorCS", {"start": v(-3.05, 2.54) * mm, "end": v(-3.17, 2.32) * mm});
            skLineSegment(sketch, "E226.MirrorCS", {"start": v(-5.08, 2.54) * mm, "end": v(-5.2, 2.32) * mm});
            skLineSegment(sketch, "E227.MirrorCS", {"start": v(6.48, 2.32) * mm, "end": v(6.35, 2.54) * mm});
            skLineSegment(sketch, "E228.MirrorCS", {"start": v(3.56, 2.54) * mm, "end": v(3.43, 2.32) * mm});
            skLineSegment(sketch, "E229.MirrorCS", {"start": v(-7.37, 2.54) * mm, "end": v(-7.5, 2.32) * mm});
            skLineSegment(sketch, "E230.MirrorCS", {"start": v(10.16, 2.54) * mm, "end": v(10.03, 2.32) * mm});
            skLineSegment(sketch, "E231.MirrorCS", {"start": v(22.86, 2.54) * mm, "end": v(22.73, 2.32) * mm});
            skLineSegment(sketch, "E232.MirrorCS", {"start": v(23.75, 2.32) * mm, "end": v(23.62, 2.54) * mm});
            skLineSegment(sketch, "E233.MirrorCS", {"start": v(-24, 2.32) * mm, "end": v(-24.13, 2.54) * mm});
            skLineSegment(sketch, "E234.MirrorCS", {"start": v(4.57, 2.54) * mm, "end": v(4.45, 2.32) * mm});
            skLineSegment(sketch, "E235.MirrorCS", {"start": v(-1.02, 2.54) * mm, "end": v(-1.14, 2.32) * mm});
            skLineSegment(sketch, "E236.MirrorCS", {"start": v(-12.06, 2.32) * mm, "end": v(-12.2, 2.54) * mm});
            skLineSegment(sketch, "E237.MirrorCS", {"start": v(-3.68, 2.32) * mm, "end": v(-3.8, 2.54) * mm});
            skLineSegment(sketch, "E238.MirrorCS", {"start": v(14.1, 2.32) * mm, "end": v(13.97, 2.54) * mm});
            skLineSegment(sketch, "E239.MirrorCS", {"start": v(14.86, 2.32) * mm, "end": v(14.73, 2.54) * mm});
            skLineSegment(sketch, "E240.MirrorCS", {"start": v(-5.84, 2.54) * mm, "end": v(-5.97, 2.32) * mm});
            skLineSegment(sketch, "E241.MirrorCS", {"start": v(-4.06, 2.54) * mm, "end": v(-4.2, 2.32) * mm});
            skLineSegment(sketch, "E242.MirrorCS", {"start": v(6.99, 2.32) * mm, "end": v(6.86, 2.54) * mm});
            skLineSegment(sketch, "E243.MirrorCS", {"start": v(13.84, 2.32) * mm, "end": v(13.72, 2.54) * mm});
            skLineSegment(sketch, "E244.MirrorCS", {"start": v(-0.89, 2.32) * mm, "end": v(-1.02, 2.54) * mm});
            skLineSegment(sketch, "E245.MirrorCS", {"start": v(-20.32, 2.54) * mm, "end": v(-20.45, 2.32) * mm});
            skLineSegment(sketch, "E246.MirrorCS", {"start": v(-5.2, 2.32) * mm, "end": v(-5.33, 2.54) * mm});
            skLineSegment(sketch, "E247.MirrorCS", {"start": v(-24.26, 2.32) * mm, "end": v(-24.38, 2.54) * mm});
            skLineSegment(sketch, "E248.MirrorCS", {"start": v(-24.64, 2.54) * mm, "end": v(-24.76, 2.32) * mm});
            skLineSegment(sketch, "E249.MirrorCS", {"start": v(14.99, 2.54) * mm, "end": v(14.86, 2.32) * mm});
            skLineSegment(sketch, "E250.MirrorCS", {"start": v(-2.67, 2.32) * mm, "end": v(-2.8, 2.54) * mm});
            skLineSegment(sketch, "E251.MirrorCS", {"start": v(15.75, 2.54) * mm, "end": v(15.62, 2.32) * mm});
            skLineSegment(sketch, "E252.MirrorCS", {"start": v(-2.03, 2.54) * mm, "end": v(-2.16, 2.32) * mm});
            skLineSegment(sketch, "E253.MirrorCS", {"start": v(17.65, 2.32) * mm, "end": v(17.53, 2.54) * mm});
            skLineSegment(sketch, "E254.MirrorCS", {"start": v(-17.78, 2.54) * mm, "end": v(-17.9, 2.32) * mm});
            skLineSegment(sketch, "E255.MirrorCS", {"start": v(13.46, 2.54) * mm, "end": v(13.34, 2.32) * mm});
            skLineSegment(sketch, "E256.MirrorCS", {"start": v(-21.97, 2.32) * mm, "end": v(-22.1, 2.54) * mm});
            skLineSegment(sketch, "E257.MirrorCS", {"start": v(-4.83, 2.54) * mm, "end": v(-4.95, 2.32) * mm});
            skLineSegment(sketch, "E258.MirrorCS", {"start": v(21.08, 2.54) * mm, "end": v(20.96, 2.32) * mm});
            skLineSegment(sketch, "E259.MirrorCS", {"start": v(5.08, 2.54) * mm, "end": v(4.95, 2.32) * mm});
            skLineSegment(sketch, "E260.MirrorCS", {"start": v(-7.75, 2.32) * mm, "end": v(-7.87, 2.54) * mm});
            skLineSegment(sketch, "E261.MirrorCS", {"start": v(-14.6, 2.32) * mm, "end": v(-14.73, 2.54) * mm});
            skLineSegment(sketch, "E262.MirrorCS", {"start": v(12.32, 2.32) * mm, "end": v(12.2, 2.54) * mm});
            skLineSegment(sketch, "E263.MirrorCS", {"start": v(11.43, 2.54) * mm, "end": v(11.3, 2.32) * mm});
            skLineSegment(sketch, "E264.MirrorCS", {"start": v(18.29, 2.54) * mm, "end": v(18.16, 2.32) * mm});
            skLineSegment(sketch, "E265.MirrorCS", {"start": v(-5.33, 2.54) * mm, "end": v(-5.46, 2.32) * mm});
            skLineSegment(sketch, "E266.MirrorCS", {"start": v(8.76, 2.32) * mm, "end": v(8.64, 2.54) * mm});
            skLineSegment(sketch, "E267.MirrorCS", {"start": v(4.32, 2.54) * mm, "end": v(4.2, 2.32) * mm});
            skLineSegment(sketch, "E268.MirrorCS", {"start": v(-10.29, 2.32) * mm, "end": v(-10.41, 2.54) * mm});
            skLineSegment(sketch, "E269.MirrorCS", {"start": v(22.35, 2.54) * mm, "end": v(22.23, 2.32) * mm});
            skLineSegment(sketch, "E270.MirrorCS", {"start": v(9.65, 2.54) * mm, "end": v(9.53, 2.32) * mm});
            skLineSegment(sketch, "E271.MirrorCS", {"start": v(-21.72, 2.32) * mm, "end": v(-21.84, 2.54) * mm});
            skLineSegment(sketch, "E272.MirrorCS", {"start": v(-11.18, 2.54) * mm, "end": v(-11.3, 2.32) * mm});
            skLineSegment(sketch, "E273.MirrorCS", {"start": v(24.13, 2.54) * mm, "end": v(24, 2.32) * mm});
            skLineSegment(sketch, "E274.MirrorCS", {"start": v(9.14, 2.54) * mm, "end": v(9.02, 2.32) * mm});
            skLineSegment(sketch, "E275.MirrorCS", {"start": v(-11.3, 2.32) * mm, "end": v(-11.43, 2.54) * mm});
            skLineSegment(sketch, "E276.MirrorCS", {"start": v(18.54, 2.54) * mm, "end": v(18.42, 2.32) * mm});
            skLineSegment(sketch, "E277.MirrorCS", {"start": v(9.53, 2.32) * mm, "end": v(9.4, 2.54) * mm});
            skLineSegment(sketch, "E278.MirrorCS", {"start": v(17.9, 2.32) * mm, "end": v(17.78, 2.54) * mm});
            skLineSegment(sketch, "E279.MirrorCS", {"start": v(13.59, 2.32) * mm, "end": v(13.46, 2.54) * mm});
            skLineSegment(sketch, "E280.MirrorCS", {"start": v(-6.48, 2.32) * mm, "end": v(-6.6, 2.54) * mm});
            skLineSegment(sketch, "E281.MirrorCS", {"start": v(-5.59, 2.54) * mm, "end": v(-5.71, 2.32) * mm});
            skLineSegment(sketch, "E282.MirrorCS", {"start": v(2.92, 2.32) * mm, "end": v(2.8, 2.54) * mm});
            skLineSegment(sketch, "E283.MirrorCS", {"start": v(6.22, 2.32) * mm, "end": v(6.1, 2.54) * mm});
            skLineSegment(sketch, "E284.MirrorCS", {"start": v(-12.95, 2.54) * mm, "end": v(-13.08, 2.32) * mm});
            skLineSegment(sketch, "E285.MirrorCS", {"start": v(23.62, 2.54) * mm, "end": v(23.5, 2.32) * mm});
            skLineSegment(sketch, "E286.MirrorCS", {"start": v(15.24, 2.54) * mm, "end": v(15.11, 2.32) * mm});
            skLineSegment(sketch, "E287.MirrorCS", {"start": v(-3.3, 2.54) * mm, "end": v(-3.43, 2.32) * mm});
            skLineSegment(sketch, "E288.MirrorCS", {"start": v(-0.76, 2.54) * mm, "end": v(-0.89, 2.32) * mm});
            skLineSegment(sketch, "E289.MirrorCS", {"start": v(16.9, 2.32) * mm, "end": v(16.76, 2.54) * mm});
            skLineSegment(sketch, "E290.MirrorCS", {"start": v(-10.03, 2.32) * mm, "end": v(-10.16, 2.54) * mm});
            skLineSegment(sketch, "E291.MirrorCS", {"start": v(16.26, 2.54) * mm, "end": v(16.13, 2.32) * mm});
            skLineSegment(sketch, "E292.MirrorCS", {"start": v(-9.78, 2.32) * mm, "end": v(-9.9, 2.54) * mm});
            skLineSegment(sketch, "E293.MirrorCS", {"start": v(-16.26, 2.54) * mm, "end": v(-16.38, 2.32) * mm});
            skLineSegment(sketch, "E294.MirrorCS", {"start": v(-8.25, 2.32) * mm, "end": v(-8.38, 2.54) * mm});
            skLineSegment(sketch, "E295.MirrorCS", {"start": v(20.96, 2.32) * mm, "end": v(20.83, 2.54) * mm});
            skLineSegment(sketch, "E296.MirrorCS", {"start": v(9.4, 2.54) * mm, "end": v(9.27, 2.32) * mm});
            skLineSegment(sketch, "E297.MirrorCS", {"start": v(23.88, 2.54) * mm, "end": v(23.75, 2.32) * mm});
            skLineSegment(sketch, "E298.MirrorCS", {"start": v(17.27, 2.54) * mm, "end": v(17.15, 2.32) * mm});
            skLineSegment(sketch, "E299.MirrorCS", {"start": v(-3.56, 2.54) * mm, "end": v(-3.68, 2.32) * mm});
            skLineSegment(sketch, "E300.MirrorCS", {"start": v(-17.4, 2.32) * mm, "end": v(-17.53, 2.54) * mm});
            skLineSegment(sketch, "E301.MirrorCS", {"start": v(-13.08, 2.32) * mm, "end": v(-13.2, 2.54) * mm});
            skLineSegment(sketch, "E302.MirrorCS", {"start": v(-19.05, 2.54) * mm, "end": v(-19.18, 2.32) * mm});
            skLineSegment(sketch, "E303.MirrorCS", {"start": v(10.41, 2.54) * mm, "end": v(10.29, 2.32) * mm});
            skLineSegment(sketch, "E304.MirrorCS", {"start": v(19.81, 2.54) * mm, "end": v(19.69, 2.32) * mm});
            skLineSegment(sketch, "E305.MirrorCS", {"start": v(-20.2, 2.32) * mm, "end": v(-20.32, 2.54) * mm});
            skLineSegment(sketch, "E306.MirrorCS", {"start": v(-7.62, 2.54) * mm, "end": v(-7.75, 2.32) * mm});
            skLineSegment(sketch, "E307.MirrorCS", {"start": v(-13.84, 2.32) * mm, "end": v(-13.97, 2.54) * mm});
            skLineSegment(sketch, "E308.MirrorCS", {"start": v(-12.57, 2.32) * mm, "end": v(-12.7, 2.54) * mm});
            skLineSegment(sketch, "E309.MirrorCS", {"start": v(-9.4, 2.54) * mm, "end": v(-9.52, 2.32) * mm});
            skLineSegment(sketch, "E310.MirrorCS", {"start": v(5.59, 2.54) * mm, "end": v(5.46, 2.32) * mm});
            skLineSegment(sketch, "E311.MirrorCS", {"start": v(21.72, 2.32) * mm, "end": v(21.6, 2.54) * mm});
            skLineSegment(sketch, "E312.MirrorCS", {"start": v(-15.37, 2.32) * mm, "end": v(-15.5, 2.54) * mm});
            skLineSegment(sketch, "E313.MirrorCS", {"start": v(22.23, 2.32) * mm, "end": v(22.1, 2.54) * mm});
            skLineSegment(sketch, "E314.MirrorCS", {"start": v(-6.1, 2.54) * mm, "end": v(-6.22, 2.32) * mm});
            skLineSegment(sketch, "E315.MirrorCS", {"start": v(-23.75, 2.32) * mm, "end": v(-23.88, 2.54) * mm});
            skLineSegment(sketch, "E316.MirrorCS", {"start": v(-3.17, 2.32) * mm, "end": v(-3.3, 2.54) * mm});
            skLineSegment(sketch, "E317.MirrorCS", {"start": v(19.05, 2.54) * mm, "end": v(18.92, 2.32) * mm});
            skLineSegment(sketch, "E318.MirrorCS", {"start": v(-12.32, 2.32) * mm, "end": v(-12.45, 2.54) * mm});
            skLineSegment(sketch, "E319.MirrorCS", {"start": v(-10.8, 2.32) * mm, "end": v(-10.92, 2.54) * mm});
            skLineSegment(sketch, "E320.MirrorCS", {"start": v(-22.35, 2.54) * mm, "end": v(-22.48, 2.32) * mm});
            skLineSegment(sketch, "E321.MirrorCS", {"start": v(6.1, 2.54) * mm, "end": v(5.97, 2.32) * mm});
            skLineSegment(sketch, "E322.MirrorCS", {"start": v(-15.5, 2.54) * mm, "end": v(-15.62, 2.32) * mm});
            skLineSegment(sketch, "E323.MirrorCS", {"start": v(-6.98, 2.32) * mm, "end": v(-7.11, 2.54) * mm});
            skLineSegment(sketch, "E324.MirrorCS", {"start": v(-4.7, 2.32) * mm, "end": v(-4.83, 2.54) * mm});
            skLineSegment(sketch, "E325.MirrorCS", {"start": v(22.48, 2.32) * mm, "end": v(22.35, 2.54) * mm});
            skLineSegment(sketch, "E326.MirrorCS", {"start": v(22.73, 2.32) * mm, "end": v(22.6, 2.54) * mm});
            skLineSegment(sketch, "E327.MirrorCS", {"start": v(-5.71, 2.32) * mm, "end": v(-5.84, 2.54) * mm});
            skLineSegment(sketch, "E328.MirrorCS", {"start": v(-2.16, 2.32) * mm, "end": v(-2.29, 2.54) * mm});
            skLineSegment(sketch, "E329.MirrorCS", {"start": v(22.1, 2.54) * mm, "end": v(21.97, 2.32) * mm});
            skLineSegment(sketch, "E330.MirrorCS", {"start": v(-10.16, 2.54) * mm, "end": v(-10.29, 2.32) * mm});
            skLineSegment(sketch, "E331.MirrorCS", {"start": v(-18.29, 2.54) * mm, "end": v(-18.41, 2.32) * mm});
            skLineSegment(sketch, "E332.MirrorCS", {"start": v(-15.75, 2.54) * mm, "end": v(-15.87, 2.32) * mm});
            skLineSegment(sketch, "E333.MirrorCS", {"start": v(9.9, 2.54) * mm, "end": v(9.78, 2.32) * mm});
            skLineSegment(sketch, "E334.MirrorCS", {"start": v(-13.46, 2.54) * mm, "end": v(-13.59, 2.32) * mm});
            skLineSegment(sketch, "E335.MirrorCS", {"start": v(-5.97, 2.32) * mm, "end": v(-6.1, 2.54) * mm});
            skLineSegment(sketch, "E336.MirrorCS", {"start": v(-8.5, 2.32) * mm, "end": v(-8.64, 2.54) * mm});
            skLineSegment(sketch, "E337.MirrorCS", {"start": v(-22.22, 2.32) * mm, "end": v(-22.35, 2.54) * mm});
            skLineSegment(sketch, "E338.MirrorCS", {"start": v(-18.54, 2.54) * mm, "end": v(-18.67, 2.32) * mm});
            skLineSegment(sketch, "E339.MirrorCS", {"start": v(-13.33, 2.32) * mm, "end": v(-13.46, 2.54) * mm});
            skLineSegment(sketch, "E340.MirrorCS", {"start": v(-24.38, 2.54) * mm, "end": v(-24.51, 2.32) * mm});
            skLineSegment(sketch, "E341.MirrorCS", {"start": v(-18.67, 2.32) * mm, "end": v(-18.8, 2.54) * mm});
            skLineSegment(sketch, "E342.MirrorCS", {"start": v(21.34, 2.54) * mm, "end": v(21.2, 2.32) * mm});
            skLineSegment(sketch, "E343.MirrorCS", {"start": v(-14.35, 2.32) * mm, "end": v(-14.48, 2.54) * mm});
            skLineSegment(sketch, "E344.MirrorCS", {"start": v(-17.65, 2.32) * mm, "end": v(-17.78, 2.54) * mm});
            skLineSegment(sketch, "E345.MirrorCS", {"start": v(13.2, 2.54) * mm, "end": v(13.08, 2.32) * mm});
            skLineSegment(sketch, "E346.MirrorCS", {"start": v(13.34, 2.32) * mm, "end": v(13.2, 2.54) * mm});
            skLineSegment(sketch, "E347.MirrorCS", {"start": v(3.18, 2.32) * mm, "end": v(3.05, 2.54) * mm});
            skLineSegment(sketch, "E348.MirrorCS", {"start": v(-15.87, 2.32) * mm, "end": v(-16, 2.54) * mm});
            skLineSegment(sketch, "E349.MirrorCS", {"start": v(-14.1, 2.32) * mm, "end": v(-14.22, 2.54) * mm});
            skLineSegment(sketch, "E350.MirrorCS", {"start": v(4.2, 2.32) * mm, "end": v(4.06, 2.54) * mm});
            skLineSegment(sketch, "E351.MirrorCS", {"start": v(23.5, 2.32) * mm, "end": v(23.37, 2.54) * mm});
            skLineSegment(sketch, "E352.MirrorCS", {"start": v(1.14, 2.32) * mm, "end": v(1.02, 2.54) * mm});
            skLineSegment(sketch, "E353.MirrorCS", {"start": v(0.5, 2.54) * mm, "end": v(0.38, 2.32) * mm});
            skLineSegment(sketch, "E354.MirrorCS", {"start": v(-14.99, 2.54) * mm, "end": v(-15.11, 2.32) * mm});
            skLineSegment(sketch, "E355.MirrorCS", {"start": v(1.9, 2.32) * mm, "end": v(1.78, 2.54) * mm});
            skLineSegment(sketch, "E356.MirrorCS", {"start": v(3.81, 2.54) * mm, "end": v(3.68, 2.32) * mm});
            skLineSegment(sketch, "E357.MirrorCS", {"start": v(1.52, 2.54) * mm, "end": v(1.4, 2.32) * mm});
            skLineSegment(sketch, "E358.MirrorCS", {"start": v(24.51, 2.32) * mm, "end": v(24.38, 2.54) * mm});
            skLineSegment(sketch, "E359.MirrorCS", {"start": v(24.26, 2.32) * mm, "end": v(24.13, 2.54) * mm});
            skLineSegment(sketch, "E360.MirrorCS", {"start": v(1.4, 2.32) * mm, "end": v(1.27, 2.54) * mm});
            skLineSegment(sketch, "E361.MirrorCS", {"start": v(-7.11, 2.54) * mm, "end": v(-7.24, 2.32) * mm});
            skLineSegment(sketch, "E362.MirrorCS", {"start": v(3.68, 2.32) * mm, "end": v(3.56, 2.54) * mm});
            skLineSegment(sketch, "E363.MirrorCS", {"start": v(1.78, 2.54) * mm, "end": v(1.65, 2.32) * mm});
            skLineSegment(sketch, "E364.MirrorCS", {"start": v(-15.24, 2.54) * mm, "end": v(-15.37, 2.32) * mm});
            skLineSegment(sketch, "E365.MirrorCS", {"start": v(19.94, 2.32) * mm, "end": v(19.81, 2.54) * mm});
            skLineSegment(sketch, "E366.MirrorCS", {"start": v(-9.02, 2.32) * mm, "end": v(-9.14, 2.54) * mm});
            skLineSegment(sketch, "E367.MirrorCS", {"start": v(19.56, 2.54) * mm, "end": v(19.43, 2.32) * mm});
            skLineSegment(sketch, "E368.MirrorCS", {"start": v(10.03, 2.32) * mm, "end": v(9.9, 2.54) * mm});
            skLineSegment(sketch, "E369.MirrorCS", {"start": v(3.94, 2.32) * mm, "end": v(3.81, 2.54) * mm});
            skLineSegment(sketch, "E370.MirrorCS", {"start": v(24.64, 2.54) * mm, "end": v(24.51, 2.32) * mm});
            skLineSegment(sketch, "E371.MirrorCS", {"start": v(-19.18, 2.32) * mm, "end": v(-19.3, 2.54) * mm});
            skLineSegment(sketch, "E372.MirrorCS", {"start": v(-23.5, 2.32) * mm, "end": v(-23.62, 2.54) * mm});
            skLineSegment(sketch, "E373.MirrorCS", {"start": v(19.43, 2.32) * mm, "end": v(19.3, 2.54) * mm});
            skLineSegment(sketch, "E374.MirrorCS", {"start": v(-9.14, 2.54) * mm, "end": v(-9.27, 2.32) * mm});
            skLineSegment(sketch, "E375.MirrorCS", {"start": v(21.46, 2.32) * mm, "end": v(21.34, 2.54) * mm});
            skLineSegment(sketch, "E376.MirrorCS", {"start": v(11.94, 2.54) * mm, "end": v(11.81, 2.32) * mm});
            skLineSegment(sketch, "E377.MirrorCS", {"start": v(23.37, 2.54) * mm, "end": v(23.24, 2.32) * mm});
            skLineSegment(sketch, "E378.MirrorCS", {"start": v(11.81, 2.32) * mm, "end": v(11.68, 2.54) * mm});
            skLineSegment(sketch, "E379.MirrorCS", {"start": v(24.9, 2.54) * mm, "end": v(24.77, 2.32) * mm});
            skLineSegment(sketch, "E380.MirrorCS", {"start": v(1.02, 2.54) * mm, "end": v(0.89, 2.32) * mm});
            skLineSegment(sketch, "E381.MirrorCS", {"start": v(-6.86, 2.54) * mm, "end": v(-6.98, 2.32) * mm});
            skLineSegment(sketch, "E382.MirrorCS", {"start": v(-19.43, 2.32) * mm, "end": v(-19.56, 2.54) * mm});
            skLineSegment(sketch, "E383.MirrorCS", {"start": v(24.9, 2.8) * mm, "end": v(24.9, 2.54) * mm});
            skLineSegment(sketch, "E384.MirrorCS", {"start": v(0.38, 2.32) * mm, "end": v(0.25, 2.54) * mm});
            skLineSegment(sketch, "E385.MirrorCS", {"start": v(10.29, 2.32) * mm, "end": v(10.16, 2.54) * mm});
            skLineSegment(sketch, "E386.MirrorCS", {"start": v(0.76, 2.54) * mm, "end": v(0.64, 2.32) * mm});
            skLineSegment(sketch, "E387.MirrorCS", {"start": v(24.38, 2.54) * mm, "end": v(24.26, 2.32) * mm});
            skLineSegment(sketch, "E388.MirrorCS", {"start": v(-24.76, 2.32) * mm, "end": v(-24.9, 2.54) * mm});
            skLineSegment(sketch, "E389.MirrorCS", {"start": v(2.16, 2.32) * mm, "end": v(2.03, 2.54) * mm});
            skLineSegment(sketch, "E390.MirrorCS", {"start": v(19.69, 2.32) * mm, "end": v(19.56, 2.54) * mm});
            skLineSegment(sketch, "E391.MirrorCS", {"start": v(24.77, 2.32) * mm, "end": v(24.64, 2.54) * mm});
            skLineSegment(sketch, "E392.MirrorCS", {"start": v(-8.89, 2.54) * mm, "end": v(-9.02, 2.32) * mm});
            skLineSegment(sketch, "E393.MirrorCS", {"start": v(-13.2, 2.54) * mm, "end": v(-13.33, 2.32) * mm});
            skLineSegment(sketch, "E394.MirrorCS", {"start": v(-19.68, 2.32) * mm, "end": v(-19.81, 2.54) * mm});
            skLineSegment(sketch, "E395.MirrorCS", {"start": v(-10.92, 2.54) * mm, "end": v(-11.05, 2.32) * mm});
            skLineSegment(sketch, "E396.MirrorCS", {"start": v(5.97, 2.32) * mm, "end": v(5.84, 2.54) * mm});
            skLineSegment(sketch, "E397.MirrorCS", {"start": v(1.27, 2.54) * mm, "end": v(1.14, 2.32) * mm});
            skLineSegment(sketch, "E398.MirrorCS", {"start": v(12.2, 2.54) * mm, "end": v(12.07, 2.32) * mm});
            skLineSegment(sketch, "E399.MirrorCS", {"start": v(5.72, 2.32) * mm, "end": v(5.59, 2.54) * mm});
            skLineSegment(sketch, "E400.MirrorCS", {"start": v(19.18, 2.32) * mm, "end": v(19.05, 2.54) * mm});
            skLineSegment(sketch, "E401.MirrorCS", {"start": v(-19.56, 2.54) * mm, "end": v(-19.68, 2.32) * mm});
            skLineSegment(sketch, "E402.MirrorCS", {"start": v(2.03, 2.54) * mm, "end": v(1.9, 2.32) * mm});
            skLineSegment(sketch, "E403.MirrorCS", {"start": v(21.2, 2.32) * mm, "end": v(21.08, 2.54) * mm});
            skLineSegment(sketch, "E404.MirrorCS", {"start": v(0.89, 2.32) * mm, "end": v(0.76, 2.54) * mm});
            skLineSegment(sketch, "E405.MirrorCS", {"start": v(0.64, 2.32) * mm, "end": v(0.5, 2.54) * mm});
            skLineSegment(sketch, "E406.MirrorCS", {"start": v(12.07, 2.32) * mm, "end": v(11.94, 2.54) * mm});
            skLineSegment(sketch, "E407.MirrorCS", {"start": v(23.24, 2.32) * mm, "end": v(23.11, 2.54) * mm});
            skLineSegment(sketch, "E408.MirrorCS", {"start": v(-24.9, 2.8) * mm, "end": v(24.9, 2.8) * mm});
            skLineSegment(sketch, "E409.MirrorCS", {"start": v(-24.9, 2.54) * mm, "end": v(-24.9, 2.8) * mm});
            skSolve(sketch);
        }
        {
            var Q0;
            Q0 = qSketchRegion(id + "F2", true);
            extrude(context, id + "F3", {"entities" : qUnion([Q0]), "operationType" : NewBodyOperationType.REMOVE, "endBound" : BoundingType.SYMMETRIC, "oppositeDirection" : true, "depth" : 25.4 * mm, "offsetDistance" : 25.4 * mm});
        }
        {
            var Q0;
            Q0=makeQuery(id+"F1.opExtrude","CAP_EDGE",EDGE,{"disambiguationData":[OSD([sQuery(id+"F0.wireOp",EDGE,"E0.left")])],"isStart":false});
            var Q1;
            Q1=makeQuery(id+"F1.opExtrude","CAP_EDGE",EDGE,{"disambiguationData":[OSD([sQuery(id+"F0.wireOp",EDGE,"E0.right")])],"isStart":false});
            var Q2;
            Q2=makeQuery(id+"F3.boolean.opBoolean","MERGE",EDGE,{"derivedFrom":[makeQuery(id+"F1.opExtrude","CAP_EDGE",EDGE,{"disambiguationData":[OSD([sQuery(id+"F0.wireOp",EDGE,"E0.top")])],"isStart":false})],"fromTools":[makeQuery(id+"F3.opExtrude","SWEPT_EDGE",EDGE,{"disambiguationData":[OSD([sQuery(id+"F2.wireOp",EDGE,"accb9737-dca4-4821-836c-b98c3f27e90128.MirrorCS"),sQuery(id+"F2.wireOp",EDGE,"accb9737-dca4-4821-836c-b98c3f27e901305.MirrorCS")])]})]});
            var Q3;
            Q3=makeQuery(id+"F3.boolean.opBoolean","MERGE",EDGE,{"derivedFrom":[makeQuery(id+"F1.opExtrude","CAP_EDGE",EDGE,{"disambiguationData":[OSD([sQuery(id+"F0.wireOp",EDGE,"E0.bottom")])],"isStart":false})],"fromTools":[makeQuery(id+"F3.opExtrude","SWEPT_EDGE",EDGE,{"disambiguationData":[OSD([sQuery(id+"F2.wireOp",EDGE,"E6.74.0.1"),sQuery(id+"F2.wireOp",EDGE,"E6.75.0.0")])]})]});
            var Q4;
            Q4=makeQuery(id+"F1.opExtrude","CAP_EDGE",EDGE,{"disambiguationData":[OSD([sQuery(id+"F0.wireOp",EDGE,"E0.right")])],"isStart":true});
            var Q5;
            Q5=makeQuery(id+"F3.boolean.opBoolean","MERGE",EDGE,{"derivedFrom":[makeQuery(id+"F1.opExtrude","CAP_EDGE",EDGE,{"disambiguationData":[OSD([sQuery(id+"F0.wireOp",EDGE,"E0.top")])],"isStart":true})],"fromTools":[makeQuery(id+"F3.opExtrude","SWEPT_EDGE",EDGE,{"disambiguationData":[OSD([sQuery(id+"F2.wireOp",EDGE,"accb9737-dca4-4821-836c-b98c3f27e901234.MirrorCS"),sQuery(id+"F2.wireOp",EDGE,"accb9737-dca4-4821-836c-b98c3f27e901281.MirrorCS")])]})]});
            var Q6;
            Q6=makeQuery(id+"F3.boolean.opBoolean","MERGE",EDGE,{"derivedFrom":[makeQuery(id+"F1.opExtrude","CAP_EDGE",EDGE,{"disambiguationData":[OSD([sQuery(id+"F0.wireOp",EDGE,"E0.bottom")])],"isStart":true})],"fromTools":[makeQuery(id+"F3.opExtrude","SWEPT_EDGE",EDGE,{"disambiguationData":[OSD([sQuery(id+"F2.wireOp",EDGE,"E5.0.75.0"),sQuery(id+"F2.wireOp",EDGE,"E5.3.76.0")])]})]});
            var Q7;
            Q7=makeQuery(id+"F1.opExtrude","CAP_FACE",FACE,{"disambiguationData":[OSD([sQuery(id+"F0.wireOp",EDGE,"E0.bottom"),sQuery(id+"F0.wireOp",EDGE,"E0.top"),sQuery(id+"F0.wireOp",EDGE,"E0.left"),sQuery(id+"F0.wireOp",EDGE,"E0.right")])],"isStart":true});
            fillet(context, id + "F4", {"entities" : qUnion([Q0, Q1, Q2, Q3, Q4, Q5, Q6, Q7]), "radius" : 0.25 * mm, "tangentPropagation" : true, "allowEdgeOverflow" : false});
        }
        {
            var Q0;
            Q0=makeQuery(id+"F1.opExtrude","CAP_FACE",FACE,{"disambiguationData":[OSD([sQuery(id+"F0.wireOp",EDGE,"E0.bottom"),sQuery(id+"F0.wireOp",EDGE,"E0.top"),sQuery(id+"F0.wireOp",EDGE,"E0.left"),sQuery(id+"F0.wireOp",EDGE,"E0.right")])],"isStart":true});
            var sketch = newSketch(context, id + "F5", { "sketchPlane" : qUnion([Q0])});
            skLineSegment(sketch, "E410.bottom", {"start": v(10.16, -0.63) * mm, "end": v(6.99, -0.63) * mm});
            skLineSegment(sketch, "E410.top", {"start": v(10.16, 0.64) * mm, "end": v(6.99, 0.64) * mm});
            skLineSegment(sketch, "E410.left", {"start": v(10.16, -0.63) * mm, "end": v(10.16, 0.64) * mm});
            skLineSegment(sketch, "E410.right", {"start": v(-10.16, -0.64) * mm, "end": v(-10.16, 0.63) * mm});
            skPoint(sketch, "E410.middle", {"position": v(0, 0) * mm});
            skLineSegment(sketch, "E411.bottom", {"start": v(0.64, -2.54) * mm, "end": v(-0.63, -2.54) * mm});
            skLineSegment(sketch, "E411.top", {"start": v(0.63, 2.54) * mm, "end": v(-0.64, 2.54) * mm});
            skLineSegment(sketch, "E411.left", {"start": v(0.64, -2.54) * mm, "end": v(0.64, -0.64) * mm});
            skLineSegment(sketch, "E411.right", {"start": v(-0.63, -2.54) * mm, "end": v(-0.64, -0.64) * mm});
            skLineSegment(sketch, "E412.bottom", {"start": v(-5.72, -2.54) * mm, "end": v(-6.99, -2.54) * mm});
            skLineSegment(sketch, "E412.top", {"start": v(-5.71, 2.54) * mm, "end": v(-6.99, 2.54) * mm});
            skLineSegment(sketch, "E412.left", {"start": v(-5.72, -2.54) * mm, "end": v(-5.72, -0.64) * mm});
            skLineSegment(sketch, "E412.right", {"start": v(-6.99, -2.54) * mm, "end": v(-6.99, -0.64) * mm});
            skPoint(sketch, "E412.middle", {"position": v(-6.35, 0) * mm});
            skLineSegment(sketch, "E413.bottom", {"start": v(6.99, -2.54) * mm, "end": v(5.71, -2.54) * mm});
            skLineSegment(sketch, "E413.top", {"start": v(6.99, 2.54) * mm, "end": v(5.71, 2.54) * mm});
            skLineSegment(sketch, "E413.left", {"start": v(6.98, -2.54) * mm, "end": v(6.99, -0.63) * mm});
            skLineSegment(sketch, "E413.right", {"start": v(5.71, -2.54) * mm, "end": v(5.71, -0.63) * mm});
            skPoint(sketch, "E413.middle", {"position": v(6.35, 0) * mm});
            skLineSegment(sketch, "E414.trimOffspring", {"start": v(-6.99, 0.63) * mm, "end": v(-6.99, 2.54) * mm});
            skLineSegment(sketch, "E415.trimOffspring", {"start": v(-6.99, 0.63) * mm, "end": v(-10.16, 0.63) * mm});
            skLineSegment(sketch, "E416.trimOffspring", {"start": v(-6.99, -0.64) * mm, "end": v(-10.16, -0.64) * mm});
            skLineSegment(sketch, "E417.trimOffspring", {"start": v(-5.72, 0.64) * mm, "end": v(-5.72, 2.54) * mm});
            skLineSegment(sketch, "E418.trimOffspring", {"start": v(-0.64, 0.64) * mm, "end": v(-0.64, 2.54) * mm});
            skLineSegment(sketch, "E419.trimOffspring", {"start": v(-0.64, -0.64) * mm, "end": v(-5.72, -0.64) * mm});
            skLineSegment(sketch, "E420.trimOffspring", {"start": v(-0.64, 0.64) * mm, "end": v(-5.72, 0.64) * mm});
            skLineSegment(sketch, "E421.trimOffspring", {"start": v(0.64, 0.64) * mm, "end": v(0.63, 2.54) * mm});
            skLineSegment(sketch, "E422.trimOffspring", {"start": v(5.71, 0.64) * mm, "end": v(5.71, 2.54) * mm});
            skLineSegment(sketch, "E423.trimOffspring", {"start": v(5.71, 0.64) * mm, "end": v(0.64, 0.64) * mm});
            skLineSegment(sketch, "E424.trimOffspring", {"start": v(6.99, 0.64) * mm, "end": v(6.99, 2.54) * mm});
            skLineSegment(sketch, "E425.trimOffspring", {"start": v(5.71, -0.63) * mm, "end": v(0.64, -0.64) * mm});
            skSolve(sketch);
        }
        {
            var Q0;
            Q0 = qSketchRegion(id + "F5", true);
            extrude(context, id + "F6", {"entities" : qUnion([Q0]), "operationType" : NewBodyOperationType.REMOVE, "oppositeDirection" : true, "depth" : 0.5 * mm, "offsetDistance" : 25.4 * mm});
        }
    });
